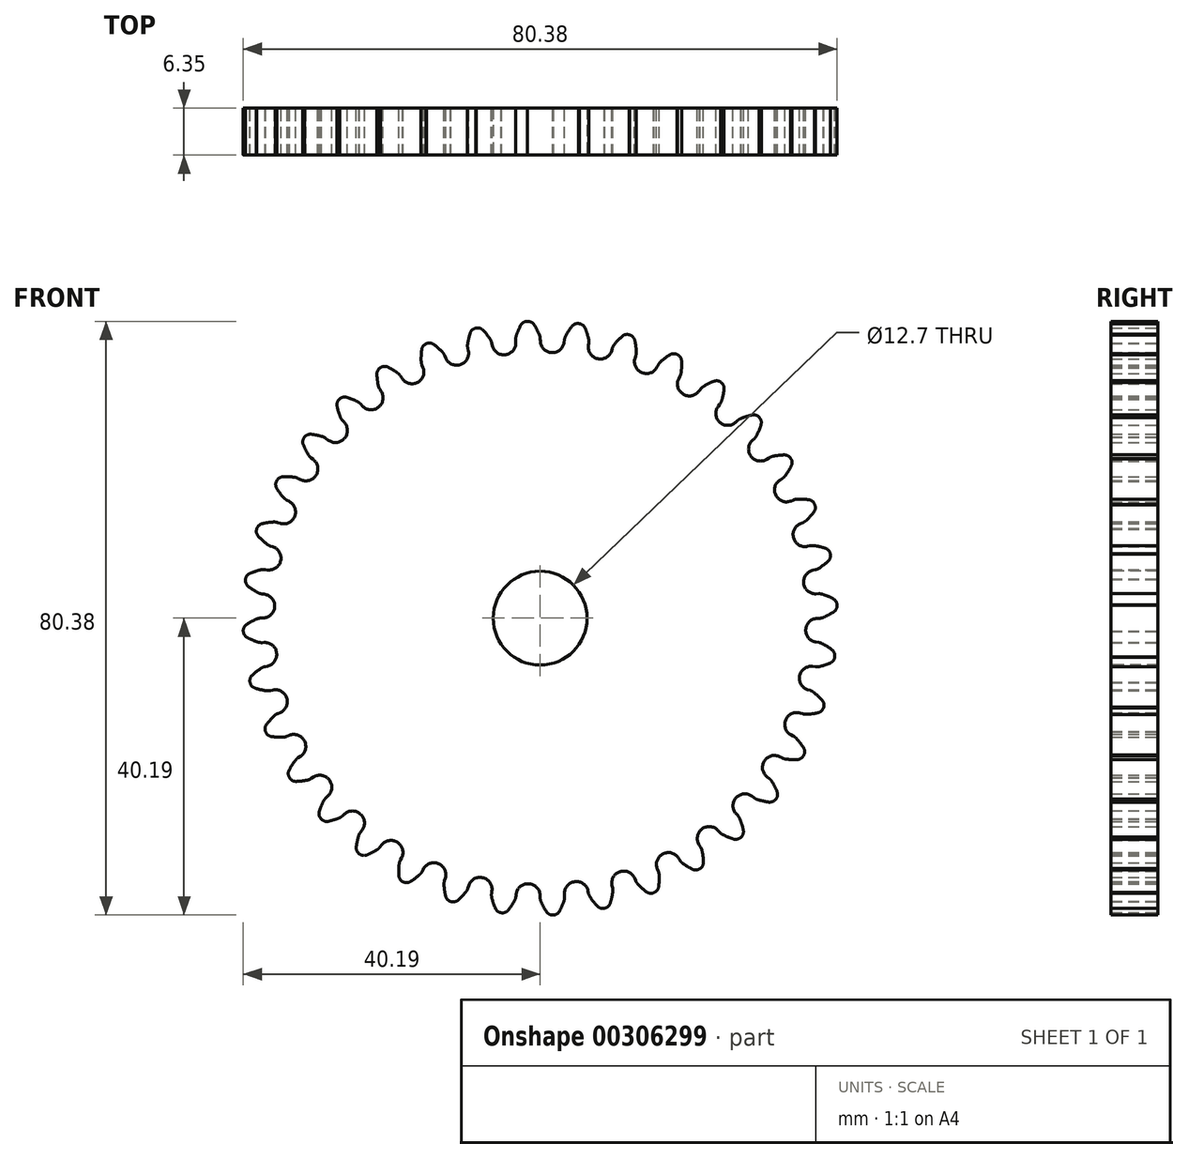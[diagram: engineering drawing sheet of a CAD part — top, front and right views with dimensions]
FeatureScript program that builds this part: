
annotation { "Feature Type Name" : "Feature", "Feature Type Description" : "" }
export const myFeature = defineFeature(function(context is Context, id is Id, definition is map)
    precondition{}
    {
        {
            var Q0;
            Q0=qCreatedBy(makeId("Front.planeOp"),FACE);
            var sketch = newSketch(context, id + "F0", { "sketchPlane" : qUnion([Q0])});
            skArc(sketch, "E0", {"start": v(-4.68, 35.67) * mm, "mid": v(-4.7, 35.67) * mm, "end": v(-4.7, 35.67) * mm});
            skArc(sketch, "E1.trimOffspring", {"start": v(-0.12, 38.39) * mm, "mid": v(-0.45, 39.07) * mm, "end": v(-0.83, 39.72) * mm});
            skLineSegment(sketch, "E2", {"start": v(-1.72, 40.19) * mm, "end": v(-1.75, 40.19) * mm});
            skLineSegment(sketch, "E3", {"start": v(0.01, 37.82) * mm, "end": v(0.03, 37.47) * mm});
            skLineSegment(sketch, "E4.MirrorCS", {"start": v(-1.8, 40.18) * mm, "end": v(-1.75, 40.19) * mm});
            skArc(sketch, "E5.MirrorCS", {"start": v(-3.23, 38.25) * mm, "mid": v(-2.96, 38.96) * mm, "end": v(-2.63, 39.64) * mm});
            skLineSegment(sketch, "E6.MirrorCS", {"start": v(-3.3, 37.67) * mm, "end": v(-3.3, 37.33) * mm});
            skPoint(sketch, "E7.visualSharp", {"position": v(-3.23, 35.83) * mm});
            skArc(sketch, "E7.filletArc", {"start": v(-4.68, 35.67) * mm, "mid": v(-3.67, 36.23) * mm, "end": v(-3.3, 37.33) * mm});
            skPoint(sketch, "E8.visualSharp", {"position": v(0.1, 35.98) * mm});
            skArc(sketch, "E8.filletArc", {"start": v(0.03, 37.47) * mm, "mid": v(0.5, 36.41) * mm, "end": v(1.56, 35.95) * mm});
            skPoint(sketch, "E9.visualSharp", {"position": v(-2.35, 40.15) * mm});
            skArc(sketch, "E9.filletArc", {"start": v(-1.8, 40.18) * mm, "mid": v(-2.28, 40.02) * mm, "end": v(-2.63, 39.64) * mm});
            skPoint(sketch, "E10.visualSharp", {"position": v(-1.16, 40.2) * mm});
            skArc(sketch, "E10.filletArc", {"start": v(-0.83, 39.72) * mm, "mid": v(-1.21, 40.07) * mm, "end": v(-1.72, 40.19) * mm});
            skPoint(sketch, "E11.visualSharp", {"position": v(0, 38.1) * mm});
            skArc(sketch, "E11.filletArc", {"start": v(0.01, 37.82) * mm, "mid": v(-0.03, 38.1) * mm, "end": v(-0.12, 38.39) * mm});
            skPoint(sketch, "E12.visualSharp", {"position": v(-3.32, 37.96) * mm});
            skArc(sketch, "E12.filletArc", {"start": v(-3.23, 38.25) * mm, "mid": v(-3.3, 37.97) * mm, "end": v(-3.3, 37.67) * mm});
            skArc(sketch, "E13.1.0", {"start": v(-6.78, 37.78) * mm, "mid": v(-7.23, 38.4) * mm, "end": v(-7.72, 38.97) * mm});
            skArc(sketch, "E13.1.1", {"start": v(-7.72, 38.97) * mm, "mid": v(-8.15, 39.25) * mm, "end": v(-8.67, 39.28) * mm});
            skArc(sketch, "E13.1.2", {"start": v(-8.74, 39.26) * mm, "mid": v(-9.2, 39.02) * mm, "end": v(-9.48, 38.58) * mm});
            skArc(sketch, "E13.1.3", {"start": v(-9.82, 37.1) * mm, "mid": v(-9.68, 37.85) * mm, "end": v(-9.48, 38.58) * mm});
            skArc(sketch, "E13.1.4", {"start": v(-10.8, 34.32) * mm, "mid": v(-9.9, 35.04) * mm, "end": v(-9.73, 36.2) * mm});
            skArc(sketch, "E13.1.5", {"start": v(-6.48, 36.9) * mm, "mid": v(-5.84, 35.95) * mm, "end": v(-4.7, 35.67) * mm});
            skArc(sketch, "E13.1.6", {"start": v(-9.82, 37.1) * mm, "mid": v(-9.84, 36.82) * mm, "end": v(-9.8, 36.53) * mm});
            skLineSegment(sketch, "E13.1.7", {"start": v(-9.8, 36.53) * mm, "end": v(-9.73, 36.2) * mm});
            skArc(sketch, "E13.1.8", {"start": v(-6.55, 37.24) * mm, "mid": v(-6.64, 37.52) * mm, "end": v(-6.78, 37.78) * mm});
            skLineSegment(sketch, "E13.1.9", {"start": v(-6.55, 37.24) * mm, "end": v(-6.48, 36.9) * mm});
            skArc(sketch, "E13.2.0", {"start": v(-13.24, 36.03) * mm, "mid": v(-13.78, 36.56) * mm, "end": v(-14.37, 37.04) * mm});
            skArc(sketch, "E13.2.1", {"start": v(-14.37, 37.04) * mm, "mid": v(-14.84, 37.24) * mm, "end": v(-15.36, 37.18) * mm});
            skArc(sketch, "E13.2.2", {"start": v(-15.43, 37.15) * mm, "mid": v(-15.84, 36.83) * mm, "end": v(-16.03, 36.35) * mm});
            skArc(sketch, "E13.2.3", {"start": v(-16.11, 34.84) * mm, "mid": v(-16.1, 35.6) * mm, "end": v(-16.03, 36.35) * mm});
            skArc(sketch, "E13.2.4", {"start": v(-16.6, 31.92) * mm, "mid": v(-15.84, 32.8) * mm, "end": v(-15.86, 33.95) * mm});
            skArc(sketch, "E13.2.5", {"start": v(-12.8, 35.22) * mm, "mid": v(-11.99, 34.39) * mm, "end": v(-10.83, 34.31) * mm});
            skArc(sketch, "E13.2.6", {"start": v(-16.11, 34.84) * mm, "mid": v(-16.08, 34.55) * mm, "end": v(-16, 34.27) * mm});
            skLineSegment(sketch, "E13.2.7", {"start": v(-16, 34.27) * mm, "end": v(-15.86, 33.95) * mm});
            skArc(sketch, "E13.2.8", {"start": v(-12.92, 35.54) * mm, "mid": v(-13.06, 35.8) * mm, "end": v(-13.24, 36.03) * mm});
            skLineSegment(sketch, "E13.2.9", {"start": v(-12.92, 35.54) * mm, "end": v(-12.8, 35.22) * mm});
            skArc(sketch, "E13.3.0", {"start": v(-19.3, 33.18) * mm, "mid": v(-19.92, 33.6) * mm, "end": v(-20.58, 33.98) * mm});
            skArc(sketch, "E13.3.1", {"start": v(-20.58, 33.98) * mm, "mid": v(-21.09, 34.1) * mm, "end": v(-21.58, 33.95) * mm});
            skArc(sketch, "E13.3.2", {"start": v(-21.64, 33.9) * mm, "mid": v(-22, 33.52) * mm, "end": v(-22.1, 33.01) * mm});
            skArc(sketch, "E13.3.3", {"start": v(-21.92, 31.51) * mm, "mid": v(-22.04, 32.26) * mm, "end": v(-22.1, 33.01) * mm});
            skArc(sketch, "E13.3.4", {"start": v(-21.9, 28.55) * mm, "mid": v(-21.3, 29.54) * mm, "end": v(-21.52, 30.68) * mm});
            skArc(sketch, "E13.3.5", {"start": v(-18.71, 32.47) * mm, "mid": v(-17.78, 31.78) * mm, "end": v(-16.62, 31.9) * mm});
            skArc(sketch, "E13.3.6", {"start": v(-21.92, 31.51) * mm, "mid": v(-21.84, 31.23) * mm, "end": v(-21.7, 30.97) * mm});
            skLineSegment(sketch, "E13.3.7", {"start": v(-21.7, 30.97) * mm, "end": v(-21.52, 30.68) * mm});
            skArc(sketch, "E13.3.8", {"start": v(-18.9, 32.76) * mm, "mid": v(-19.08, 32.99) * mm, "end": v(-19.3, 33.18) * mm});
            skLineSegment(sketch, "E13.3.9", {"start": v(-18.9, 32.76) * mm, "end": v(-18.71, 32.47) * mm});
            skArc(sketch, "E13.4.0", {"start": v(-24.77, 29.33) * mm, "mid": v(-25.46, 29.64) * mm, "end": v(-26.17, 29.9) * mm});
            skArc(sketch, "E13.4.1", {"start": v(-26.17, 29.9) * mm, "mid": v(-26.69, 29.92) * mm, "end": v(-27.15, 29.68) * mm});
            skArc(sketch, "E13.4.2", {"start": v(-27.2, 29.63) * mm, "mid": v(-27.48, 29.2) * mm, "end": v(-27.5, 28.68) * mm});
            skArc(sketch, "E13.4.3", {"start": v(-27.06, 27.23) * mm, "mid": v(-27.3, 27.94) * mm, "end": v(-27.5, 28.68) * mm});
            skArc(sketch, "E13.4.4", {"start": v(-26.52, 24.32) * mm, "mid": v(-26.1, 25.4) * mm, "end": v(-26.52, 26.48) * mm});
            skArc(sketch, "E13.4.5", {"start": v(-24.07, 28.72) * mm, "mid": v(-23.03, 28.21) * mm, "end": v(-21.91, 28.54) * mm});
            skArc(sketch, "E13.4.6", {"start": v(-27.06, 27.23) * mm, "mid": v(-26.93, 26.97) * mm, "end": v(-26.75, 26.73) * mm});
            skLineSegment(sketch, "E13.4.7", {"start": v(-26.75, 26.73) * mm, "end": v(-26.52, 26.48) * mm});
            skArc(sketch, "E13.4.8", {"start": v(-24.3, 28.98) * mm, "mid": v(-24.52, 29.17) * mm, "end": v(-24.77, 29.33) * mm});
            skLineSegment(sketch, "E13.4.9", {"start": v(-24.3, 28.98) * mm, "end": v(-24.07, 28.72) * mm});
            skArc(sketch, "E13.5.0", {"start": v(-29.48, 24.58) * mm, "mid": v(-30.22, 24.77) * mm, "end": v(-30.96, 24.9) * mm});
            skArc(sketch, "E13.5.1", {"start": v(-30.96, 24.9) * mm, "mid": v(-31.48, 24.83) * mm, "end": v(-31.89, 24.52) * mm});
            skArc(sketch, "E13.5.2", {"start": v(-31.94, 24.46) * mm, "mid": v(-32.13, 23.98) * mm, "end": v(-32.06, 23.46) * mm});
            skArc(sketch, "E13.5.3", {"start": v(-31.38, 22.12) * mm, "mid": v(-31.74, 22.78) * mm, "end": v(-32.06, 23.46) * mm});
            skArc(sketch, "E13.5.4", {"start": v(-30.34, 19.34) * mm, "mid": v(-30.11, 20.48) * mm, "end": v(-30.71, 21.47) * mm});
            skArc(sketch, "E13.5.5", {"start": v(-28.69, 24.1) * mm, "mid": v(-27.58, 23.78) * mm, "end": v(-26.54, 24.3) * mm});
            skArc(sketch, "E13.5.6", {"start": v(-31.38, 22.12) * mm, "mid": v(-31.2, 21.88) * mm, "end": v(-30.98, 21.68) * mm});
            skLineSegment(sketch, "E13.5.7", {"start": v(-30.98, 21.68) * mm, "end": v(-30.71, 21.47) * mm});
            skArc(sketch, "E13.5.8", {"start": v(-28.96, 24.32) * mm, "mid": v(-29.2, 24.47) * mm, "end": v(-29.48, 24.58) * mm});
            skLineSegment(sketch, "E13.5.9", {"start": v(-28.96, 24.32) * mm, "end": v(-28.69, 24.1) * mm});
            skArc(sketch, "E13.6.0", {"start": v(-33.3, 19.09) * mm, "mid": v(-34.06, 19.14) * mm, "end": v(-34.82, 19.14) * mm});
            skArc(sketch, "E13.6.1", {"start": v(-34.82, 19.14) * mm, "mid": v(-35.3, 18.99) * mm, "end": v(-35.66, 18.6) * mm});
            skArc(sketch, "E13.6.2", {"start": v(-35.7, 18.54) * mm, "mid": v(-35.8, 18.03) * mm, "end": v(-35.65, 17.54) * mm});
            skArc(sketch, "E13.6.3", {"start": v(-34.74, 16.33) * mm, "mid": v(-35.22, 16.92) * mm, "end": v(-35.65, 17.54) * mm});
            skArc(sketch, "E13.6.4", {"start": v(-33.24, 13.78) * mm, "mid": v(-33.2, 14.94) * mm, "end": v(-33.97, 15.81) * mm});
            skArc(sketch, "E13.6.5", {"start": v(-32.44, 18.76) * mm, "mid": v(-31.29, 18.63) * mm, "end": v(-30.35, 19.32) * mm});
            skArc(sketch, "E13.6.6", {"start": v(-34.74, 16.33) * mm, "mid": v(-34.53, 16.13) * mm, "end": v(-34.28, 15.97) * mm});
            skLineSegment(sketch, "E13.6.7", {"start": v(-34.28, 15.97) * mm, "end": v(-33.97, 15.81) * mm});
            skArc(sketch, "E13.6.8", {"start": v(-32.74, 18.92) * mm, "mid": v(-33.02, 19.03) * mm, "end": v(-33.3, 19.09) * mm});
            skLineSegment(sketch, "E13.6.9", {"start": v(-32.74, 18.92) * mm, "end": v(-32.44, 18.76) * mm});
            skArc(sketch, "E13.7.0", {"start": v(-36.11, 13.02) * mm, "mid": v(-36.87, 12.94) * mm, "end": v(-37.6, 12.8) * mm});
            skArc(sketch, "E13.7.1", {"start": v(-37.6, 12.8) * mm, "mid": v(-38.07, 12.57) * mm, "end": v(-38.35, 12.13) * mm});
            skArc(sketch, "E13.7.2", {"start": v(-38.37, 12.06) * mm, "mid": v(-38.4, 11.54) * mm, "end": v(-38.15, 11.08) * mm});
            skArc(sketch, "E13.7.3", {"start": v(-37.05, 10.05) * mm, "mid": v(-37.62, 10.55) * mm, "end": v(-38.15, 11.08) * mm});
            skArc(sketch, "E13.7.4", {"start": v(-35.12, 7.8) * mm, "mid": v(-35.3, 8.95) * mm, "end": v(-36.2, 9.67) * mm});
            skArc(sketch, "E13.7.5", {"start": v(-35.2, 12.84) * mm, "mid": v(-34.05, 12.92) * mm, "end": v(-33.25, 13.76) * mm});
            skArc(sketch, "E13.7.6", {"start": v(-37.05, 10.05) * mm, "mid": v(-36.8, 9.89) * mm, "end": v(-36.53, 9.78) * mm});
            skLineSegment(sketch, "E13.7.7", {"start": v(-36.53, 9.78) * mm, "end": v(-36.2, 9.67) * mm});
            skArc(sketch, "E13.7.8", {"start": v(-35.53, 12.95) * mm, "mid": v(-35.82, 13) * mm, "end": v(-36.11, 13.02) * mm});
            skLineSegment(sketch, "E13.7.9", {"start": v(-35.53, 12.95) * mm, "end": v(-35.2, 12.84) * mm});
            skArc(sketch, "E13.8.0", {"start": v(-37.82, 6.55) * mm, "mid": v(-38.55, 6.34) * mm, "end": v(-39.26, 6.08) * mm});
            skArc(sketch, "E13.8.1", {"start": v(-39.26, 6.08) * mm, "mid": v(-39.67, 5.76) * mm, "end": v(-39.88, 5.29) * mm});
            skArc(sketch, "E13.8.2", {"start": v(-39.89, 5.21) * mm, "mid": v(-39.81, 4.7) * mm, "end": v(-39.5, 4.3) * mm});
            skArc(sketch, "E13.8.3", {"start": v(-38.23, 3.46) * mm, "mid": v(-38.88, 3.85) * mm, "end": v(-39.5, 4.3) * mm});
            skArc(sketch, "E13.8.4", {"start": v(-35.94, 1.58) * mm, "mid": v(-36.32, 2.68) * mm, "end": v(-37.33, 3.24) * mm});
            skArc(sketch, "E13.8.5", {"start": v(-36.9, 6.53) * mm, "mid": v(-35.77, 6.81) * mm, "end": v(-35.13, 7.77) * mm});
            skArc(sketch, "E13.8.6", {"start": v(-38.23, 3.46) * mm, "mid": v(-37.96, 3.35) * mm, "end": v(-37.67, 3.28) * mm});
            skLineSegment(sketch, "E13.8.7", {"start": v(-37.67, 3.28) * mm, "end": v(-37.33, 3.24) * mm});
            skArc(sketch, "E13.8.8", {"start": v(-37.24, 6.58) * mm, "mid": v(-37.53, 6.6) * mm, "end": v(-37.82, 6.55) * mm});
            skLineSegment(sketch, "E13.8.9", {"start": v(-37.24, 6.58) * mm, "end": v(-36.9, 6.53) * mm});
            skArc(sketch, "E13.9.0", {"start": v(-38.39, -0.12) * mm, "mid": v(-39.07, -0.45) * mm, "end": v(-39.72, -0.83) * mm});
            skArc(sketch, "E13.9.1", {"start": v(-39.72, -0.83) * mm, "mid": v(-40.07, -1.21) * mm, "end": v(-40.19, -1.72) * mm});
            skArc(sketch, "E13.9.2", {"start": v(-40.18, -1.8) * mm, "mid": v(-40.02, -2.28) * mm, "end": v(-39.64, -2.63) * mm});
            skArc(sketch, "E13.9.3", {"start": v(-38.25, -3.23) * mm, "mid": v(-38.96, -2.96) * mm, "end": v(-39.64, -2.63) * mm});
            skArc(sketch, "E13.9.4", {"start": v(-35.67, -4.68) * mm, "mid": v(-36.23, -3.67) * mm, "end": v(-37.33, -3.3) * mm});
            skArc(sketch, "E13.9.5", {"start": v(-37.47, 0.03) * mm, "mid": v(-36.41, 0.5) * mm, "end": v(-35.95, 1.56) * mm});
            skArc(sketch, "E13.9.6", {"start": v(-38.25, -3.23) * mm, "mid": v(-37.97, -3.3) * mm, "end": v(-37.67, -3.3) * mm});
            skLineSegment(sketch, "E13.9.7", {"start": v(-37.67, -3.3) * mm, "end": v(-37.33, -3.3) * mm});
            skArc(sketch, "E13.9.8", {"start": v(-37.82, 0.01) * mm, "mid": v(-38.1, -0.03) * mm, "end": v(-38.39, -0.12) * mm});
            skLineSegment(sketch, "E13.9.9", {"start": v(-37.82, 0.01) * mm, "end": v(-37.47, 0.03) * mm});
            skArc(sketch, "E13.10.0", {"start": v(-37.78, -6.78) * mm, "mid": v(-38.4, -7.23) * mm, "end": v(-38.97, -7.72) * mm});
            skArc(sketch, "E13.10.1", {"start": v(-38.97, -7.72) * mm, "mid": v(-39.25, -8.15) * mm, "end": v(-39.28, -8.67) * mm});
            skArc(sketch, "E13.10.2", {"start": v(-39.26, -8.74) * mm, "mid": v(-39.02, -9.2) * mm, "end": v(-38.58, -9.48) * mm});
            skArc(sketch, "E13.10.3", {"start": v(-37.1, -9.82) * mm, "mid": v(-37.85, -9.68) * mm, "end": v(-38.58, -9.48) * mm});
            skArc(sketch, "E13.10.4", {"start": v(-34.32, -10.8) * mm, "mid": v(-35.04, -9.9) * mm, "end": v(-36.2, -9.73) * mm});
            skArc(sketch, "E13.10.5", {"start": v(-36.9, -6.48) * mm, "mid": v(-35.95, -5.84) * mm, "end": v(-35.67, -4.7) * mm});
            skArc(sketch, "E13.10.6", {"start": v(-37.1, -9.82) * mm, "mid": v(-36.82, -9.84) * mm, "end": v(-36.53, -9.8) * mm});
            skLineSegment(sketch, "E13.10.7", {"start": v(-36.53, -9.8) * mm, "end": v(-36.2, -9.73) * mm});
            skArc(sketch, "E13.10.8", {"start": v(-37.24, -6.55) * mm, "mid": v(-37.52, -6.64) * mm, "end": v(-37.78, -6.78) * mm});
            skLineSegment(sketch, "E13.10.9", {"start": v(-37.24, -6.55) * mm, "end": v(-36.9, -6.48) * mm});
            skArc(sketch, "E13.11.0", {"start": v(-36.03, -13.24) * mm, "mid": v(-36.56, -13.78) * mm, "end": v(-37.04, -14.37) * mm});
            skArc(sketch, "E13.11.1", {"start": v(-37.04, -14.37) * mm, "mid": v(-37.24, -14.84) * mm, "end": v(-37.18, -15.36) * mm});
            skArc(sketch, "E13.11.2", {"start": v(-37.15, -15.43) * mm, "mid": v(-36.83, -15.84) * mm, "end": v(-36.35, -16.03) * mm});
            skArc(sketch, "E13.11.3", {"start": v(-34.84, -16.11) * mm, "mid": v(-35.6, -16.1) * mm, "end": v(-36.35, -16.03) * mm});
            skArc(sketch, "E13.11.4", {"start": v(-31.92, -16.6) * mm, "mid": v(-32.8, -15.84) * mm, "end": v(-33.95, -15.86) * mm});
            skArc(sketch, "E13.11.5", {"start": v(-35.22, -12.8) * mm, "mid": v(-34.39, -11.99) * mm, "end": v(-34.31, -10.83) * mm});
            skArc(sketch, "E13.11.6", {"start": v(-34.84, -16.11) * mm, "mid": v(-34.55, -16.08) * mm, "end": v(-34.27, -16) * mm});
            skLineSegment(sketch, "E13.11.7", {"start": v(-34.27, -16) * mm, "end": v(-33.95, -15.86) * mm});
            skArc(sketch, "E13.11.8", {"start": v(-35.54, -12.92) * mm, "mid": v(-35.8, -13.06) * mm, "end": v(-36.03, -13.24) * mm});
            skLineSegment(sketch, "E13.11.9", {"start": v(-35.54, -12.92) * mm, "end": v(-35.22, -12.8) * mm});
            skArc(sketch, "E13.12.0", {"start": v(-33.18, -19.3) * mm, "mid": v(-33.6, -19.92) * mm, "end": v(-33.98, -20.58) * mm});
            skArc(sketch, "E13.12.1", {"start": v(-33.98, -20.58) * mm, "mid": v(-34.1, -21.09) * mm, "end": v(-33.95, -21.58) * mm});
            skArc(sketch, "E13.12.2", {"start": v(-33.9, -21.64) * mm, "mid": v(-33.52, -22) * mm, "end": v(-33.01, -22.1) * mm});
            skArc(sketch, "E13.12.3", {"start": v(-31.51, -21.92) * mm, "mid": v(-32.26, -22.04) * mm, "end": v(-33.01, -22.1) * mm});
            skArc(sketch, "E13.12.4", {"start": v(-28.55, -21.9) * mm, "mid": v(-29.54, -21.3) * mm, "end": v(-30.68, -21.52) * mm});
            skArc(sketch, "E13.12.5", {"start": v(-32.47, -18.71) * mm, "mid": v(-31.78, -17.78) * mm, "end": v(-31.9, -16.62) * mm});
            skArc(sketch, "E13.12.6", {"start": v(-31.51, -21.92) * mm, "mid": v(-31.23, -21.84) * mm, "end": v(-30.97, -21.7) * mm});
            skLineSegment(sketch, "E13.12.7", {"start": v(-30.97, -21.7) * mm, "end": v(-30.68, -21.52) * mm});
            skArc(sketch, "E13.12.8", {"start": v(-32.76, -18.9) * mm, "mid": v(-32.99, -19.08) * mm, "end": v(-33.18, -19.3) * mm});
            skLineSegment(sketch, "E13.12.9", {"start": v(-32.76, -18.9) * mm, "end": v(-32.47, -18.71) * mm});
            skArc(sketch, "E13.13.0", {"start": v(-29.33, -24.77) * mm, "mid": v(-29.64, -25.46) * mm, "end": v(-29.9, -26.17) * mm});
            skArc(sketch, "E13.13.1", {"start": v(-29.9, -26.17) * mm, "mid": v(-29.92, -26.69) * mm, "end": v(-29.68, -27.15) * mm});
            skArc(sketch, "E13.13.2", {"start": v(-29.63, -27.2) * mm, "mid": v(-29.2, -27.48) * mm, "end": v(-28.68, -27.5) * mm});
            skArc(sketch, "E13.13.3", {"start": v(-27.23, -27.06) * mm, "mid": v(-27.94, -27.3) * mm, "end": v(-28.68, -27.5) * mm});
            skArc(sketch, "E13.13.4", {"start": v(-24.32, -26.52) * mm, "mid": v(-25.4, -26.1) * mm, "end": v(-26.48, -26.52) * mm});
            skArc(sketch, "E13.13.5", {"start": v(-28.72, -24.07) * mm, "mid": v(-28.21, -23.03) * mm, "end": v(-28.54, -21.91) * mm});
            skArc(sketch, "E13.13.6", {"start": v(-27.23, -27.06) * mm, "mid": v(-26.97, -26.93) * mm, "end": v(-26.73, -26.75) * mm});
            skLineSegment(sketch, "E13.13.7", {"start": v(-26.73, -26.75) * mm, "end": v(-26.48, -26.52) * mm});
            skArc(sketch, "E13.13.8", {"start": v(-28.98, -24.3) * mm, "mid": v(-29.17, -24.52) * mm, "end": v(-29.33, -24.77) * mm});
            skLineSegment(sketch, "E13.13.9", {"start": v(-28.98, -24.3) * mm, "end": v(-28.72, -24.07) * mm});
            skArc(sketch, "E13.14.0", {"start": v(-24.58, -29.48) * mm, "mid": v(-24.77, -30.22) * mm, "end": v(-24.9, -30.96) * mm});
            skArc(sketch, "E13.14.1", {"start": v(-24.9, -30.96) * mm, "mid": v(-24.83, -31.48) * mm, "end": v(-24.52, -31.89) * mm});
            skArc(sketch, "E13.14.2", {"start": v(-24.46, -31.94) * mm, "mid": v(-23.98, -32.13) * mm, "end": v(-23.46, -32.06) * mm});
            skArc(sketch, "E13.14.3", {"start": v(-22.12, -31.38) * mm, "mid": v(-22.78, -31.74) * mm, "end": v(-23.46, -32.06) * mm});
            skArc(sketch, "E13.14.4", {"start": v(-19.34, -30.34) * mm, "mid": v(-20.48, -30.11) * mm, "end": v(-21.47, -30.71) * mm});
            skArc(sketch, "E13.14.5", {"start": v(-24.1, -28.69) * mm, "mid": v(-23.78, -27.58) * mm, "end": v(-24.3, -26.54) * mm});
            skArc(sketch, "E13.14.6", {"start": v(-22.12, -31.38) * mm, "mid": v(-21.88, -31.2) * mm, "end": v(-21.68, -30.98) * mm});
            skLineSegment(sketch, "E13.14.7", {"start": v(-21.68, -30.98) * mm, "end": v(-21.47, -30.71) * mm});
            skArc(sketch, "E13.14.8", {"start": v(-24.32, -28.96) * mm, "mid": v(-24.47, -29.2) * mm, "end": v(-24.58, -29.48) * mm});
            skLineSegment(sketch, "E13.14.9", {"start": v(-24.32, -28.96) * mm, "end": v(-24.1, -28.69) * mm});
            skArc(sketch, "E13.15.0", {"start": v(-19.09, -33.3) * mm, "mid": v(-19.14, -34.06) * mm, "end": v(-19.14, -34.82) * mm});
            skArc(sketch, "E13.15.1", {"start": v(-19.14, -34.82) * mm, "mid": v(-18.99, -35.3) * mm, "end": v(-18.6, -35.66) * mm});
            skArc(sketch, "E13.15.2", {"start": v(-18.54, -35.7) * mm, "mid": v(-18.03, -35.8) * mm, "end": v(-17.54, -35.65) * mm});
            skArc(sketch, "E13.15.3", {"start": v(-16.33, -34.74) * mm, "mid": v(-16.92, -35.22) * mm, "end": v(-17.54, -35.65) * mm});
            skArc(sketch, "E13.15.4", {"start": v(-13.78, -33.24) * mm, "mid": v(-14.94, -33.2) * mm, "end": v(-15.81, -33.97) * mm});
            skArc(sketch, "E13.15.5", {"start": v(-18.76, -32.44) * mm, "mid": v(-18.63, -31.29) * mm, "end": v(-19.32, -30.35) * mm});
            skArc(sketch, "E13.15.6", {"start": v(-16.33, -34.74) * mm, "mid": v(-16.13, -34.53) * mm, "end": v(-15.97, -34.28) * mm});
            skLineSegment(sketch, "E13.15.7", {"start": v(-15.97, -34.28) * mm, "end": v(-15.81, -33.97) * mm});
            skArc(sketch, "E13.15.8", {"start": v(-18.92, -32.74) * mm, "mid": v(-19.03, -33.02) * mm, "end": v(-19.09, -33.3) * mm});
            skLineSegment(sketch, "E13.15.9", {"start": v(-18.92, -32.74) * mm, "end": v(-18.76, -32.44) * mm});
            skArc(sketch, "E13.16.0", {"start": v(-13.02, -36.11) * mm, "mid": v(-12.94, -36.87) * mm, "end": v(-12.8, -37.6) * mm});
            skArc(sketch, "E13.16.1", {"start": v(-12.8, -37.6) * mm, "mid": v(-12.57, -38.07) * mm, "end": v(-12.13, -38.35) * mm});
            skArc(sketch, "E13.16.2", {"start": v(-12.06, -38.37) * mm, "mid": v(-11.54, -38.4) * mm, "end": v(-11.08, -38.15) * mm});
            skArc(sketch, "E13.16.3", {"start": v(-10.05, -37.05) * mm, "mid": v(-10.55, -37.62) * mm, "end": v(-11.08, -38.15) * mm});
            skArc(sketch, "E13.16.4", {"start": v(-7.8, -35.12) * mm, "mid": v(-8.95, -35.3) * mm, "end": v(-9.67, -36.2) * mm});
            skArc(sketch, "E13.16.5", {"start": v(-12.84, -35.2) * mm, "mid": v(-12.92, -34.05) * mm, "end": v(-13.76, -33.25) * mm});
            skArc(sketch, "E13.16.6", {"start": v(-10.05, -37.05) * mm, "mid": v(-9.89, -36.8) * mm, "end": v(-9.78, -36.53) * mm});
            skLineSegment(sketch, "E13.16.7", {"start": v(-9.78, -36.53) * mm, "end": v(-9.67, -36.2) * mm});
            skArc(sketch, "E13.16.8", {"start": v(-12.95, -35.53) * mm, "mid": v(-13, -35.82) * mm, "end": v(-13.02, -36.11) * mm});
            skLineSegment(sketch, "E13.16.9", {"start": v(-12.95, -35.53) * mm, "end": v(-12.84, -35.2) * mm});
            skArc(sketch, "E13.17.0", {"start": v(-6.55, -37.82) * mm, "mid": v(-6.34, -38.55) * mm, "end": v(-6.08, -39.26) * mm});
            skArc(sketch, "E13.17.1", {"start": v(-6.08, -39.26) * mm, "mid": v(-5.76, -39.67) * mm, "end": v(-5.29, -39.88) * mm});
            skArc(sketch, "E13.17.2", {"start": v(-5.21, -39.89) * mm, "mid": v(-4.7, -39.81) * mm, "end": v(-4.3, -39.5) * mm});
            skArc(sketch, "E13.17.3", {"start": v(-3.46, -38.23) * mm, "mid": v(-3.85, -38.88) * mm, "end": v(-4.3, -39.5) * mm});
            skArc(sketch, "E13.17.4", {"start": v(-1.58, -35.94) * mm, "mid": v(-2.68, -36.32) * mm, "end": v(-3.24, -37.33) * mm});
            skArc(sketch, "E13.17.5", {"start": v(-6.53, -36.9) * mm, "mid": v(-6.81, -35.77) * mm, "end": v(-7.77, -35.13) * mm});
            skArc(sketch, "E13.17.6", {"start": v(-3.46, -38.23) * mm, "mid": v(-3.35, -37.96) * mm, "end": v(-3.28, -37.67) * mm});
            skLineSegment(sketch, "E13.17.7", {"start": v(-3.28, -37.67) * mm, "end": v(-3.24, -37.33) * mm});
            skArc(sketch, "E13.17.8", {"start": v(-6.58, -37.24) * mm, "mid": v(-6.6, -37.53) * mm, "end": v(-6.55, -37.82) * mm});
            skLineSegment(sketch, "E13.17.9", {"start": v(-6.58, -37.24) * mm, "end": v(-6.53, -36.9) * mm});
            skArc(sketch, "E13.18.0", {"start": v(0.12, -38.39) * mm, "mid": v(0.45, -39.07) * mm, "end": v(0.83, -39.72) * mm});
            skArc(sketch, "E13.18.1", {"start": v(0.83, -39.72) * mm, "mid": v(1.21, -40.07) * mm, "end": v(1.72, -40.19) * mm});
            skArc(sketch, "E13.18.2", {"start": v(1.8, -40.18) * mm, "mid": v(2.28, -40.02) * mm, "end": v(2.63, -39.64) * mm});
            skArc(sketch, "E13.18.3", {"start": v(3.23, -38.25) * mm, "mid": v(2.96, -38.96) * mm, "end": v(2.63, -39.64) * mm});
            skArc(sketch, "E13.18.4", {"start": v(4.68, -35.67) * mm, "mid": v(3.67, -36.23) * mm, "end": v(3.3, -37.33) * mm});
            skArc(sketch, "E13.18.5", {"start": v(-0.03, -37.47) * mm, "mid": v(-0.5, -36.41) * mm, "end": v(-1.56, -35.95) * mm});
            skArc(sketch, "E13.18.6", {"start": v(3.23, -38.25) * mm, "mid": v(3.3, -37.97) * mm, "end": v(3.3, -37.67) * mm});
            skLineSegment(sketch, "E13.18.7", {"start": v(3.3, -37.67) * mm, "end": v(3.3, -37.33) * mm});
            skArc(sketch, "E13.18.8", {"start": v(-0.01, -37.82) * mm, "mid": v(0.03, -38.1) * mm, "end": v(0.12, -38.39) * mm});
            skLineSegment(sketch, "E13.18.9", {"start": v(-0.01, -37.82) * mm, "end": v(-0.03, -37.47) * mm});
            skArc(sketch, "E13.19.0", {"start": v(6.78, -37.78) * mm, "mid": v(7.23, -38.4) * mm, "end": v(7.72, -38.97) * mm});
            skArc(sketch, "E13.19.1", {"start": v(7.72, -38.97) * mm, "mid": v(8.15, -39.25) * mm, "end": v(8.67, -39.28) * mm});
            skArc(sketch, "E13.19.2", {"start": v(8.74, -39.26) * mm, "mid": v(9.2, -39.02) * mm, "end": v(9.48, -38.58) * mm});
            skArc(sketch, "E13.19.3", {"start": v(9.82, -37.1) * mm, "mid": v(9.68, -37.85) * mm, "end": v(9.48, -38.58) * mm});
            skArc(sketch, "E13.19.4", {"start": v(10.8, -34.32) * mm, "mid": v(9.9, -35.04) * mm, "end": v(9.73, -36.2) * mm});
            skArc(sketch, "E13.19.5", {"start": v(6.48, -36.9) * mm, "mid": v(5.84, -35.95) * mm, "end": v(4.7, -35.67) * mm});
            skArc(sketch, "E13.19.6", {"start": v(9.82, -37.1) * mm, "mid": v(9.84, -36.82) * mm, "end": v(9.8, -36.53) * mm});
            skLineSegment(sketch, "E13.19.7", {"start": v(9.8, -36.53) * mm, "end": v(9.73, -36.2) * mm});
            skArc(sketch, "E13.19.8", {"start": v(6.55, -37.24) * mm, "mid": v(6.64, -37.52) * mm, "end": v(6.78, -37.78) * mm});
            skLineSegment(sketch, "E13.19.9", {"start": v(6.55, -37.24) * mm, "end": v(6.48, -36.9) * mm});
            skArc(sketch, "E13.20.0", {"start": v(13.24, -36.03) * mm, "mid": v(13.78, -36.56) * mm, "end": v(14.37, -37.04) * mm});
            skArc(sketch, "E13.20.1", {"start": v(14.37, -37.04) * mm, "mid": v(14.84, -37.24) * mm, "end": v(15.36, -37.18) * mm});
            skArc(sketch, "E13.20.2", {"start": v(15.43, -37.15) * mm, "mid": v(15.84, -36.83) * mm, "end": v(16.03, -36.35) * mm});
            skArc(sketch, "E13.20.3", {"start": v(16.11, -34.84) * mm, "mid": v(16.1, -35.6) * mm, "end": v(16.03, -36.35) * mm});
            skArc(sketch, "E13.20.4", {"start": v(16.6, -31.92) * mm, "mid": v(15.84, -32.8) * mm, "end": v(15.86, -33.95) * mm});
            skArc(sketch, "E13.20.5", {"start": v(12.8, -35.22) * mm, "mid": v(11.99, -34.39) * mm, "end": v(10.83, -34.31) * mm});
            skArc(sketch, "E13.20.6", {"start": v(16.11, -34.84) * mm, "mid": v(16.08, -34.55) * mm, "end": v(16, -34.27) * mm});
            skLineSegment(sketch, "E13.20.7", {"start": v(16, -34.27) * mm, "end": v(15.86, -33.95) * mm});
            skArc(sketch, "E13.20.8", {"start": v(12.92, -35.54) * mm, "mid": v(13.06, -35.8) * mm, "end": v(13.24, -36.03) * mm});
            skLineSegment(sketch, "E13.20.9", {"start": v(12.92, -35.54) * mm, "end": v(12.8, -35.22) * mm});
            skArc(sketch, "E13.21.0", {"start": v(19.3, -33.18) * mm, "mid": v(19.92, -33.6) * mm, "end": v(20.58, -33.98) * mm});
            skArc(sketch, "E13.21.1", {"start": v(20.58, -33.98) * mm, "mid": v(21.09, -34.1) * mm, "end": v(21.58, -33.95) * mm});
            skArc(sketch, "E13.21.2", {"start": v(21.64, -33.9) * mm, "mid": v(22, -33.52) * mm, "end": v(22.1, -33.01) * mm});
            skArc(sketch, "E13.21.3", {"start": v(21.92, -31.51) * mm, "mid": v(22.04, -32.26) * mm, "end": v(22.1, -33.01) * mm});
            skArc(sketch, "E13.21.4", {"start": v(21.9, -28.55) * mm, "mid": v(21.3, -29.54) * mm, "end": v(21.52, -30.68) * mm});
            skArc(sketch, "E13.21.5", {"start": v(18.71, -32.47) * mm, "mid": v(17.78, -31.78) * mm, "end": v(16.62, -31.9) * mm});
            skArc(sketch, "E13.21.6", {"start": v(21.92, -31.51) * mm, "mid": v(21.84, -31.23) * mm, "end": v(21.7, -30.97) * mm});
            skLineSegment(sketch, "E13.21.7", {"start": v(21.7, -30.97) * mm, "end": v(21.52, -30.68) * mm});
            skArc(sketch, "E13.21.8", {"start": v(18.9, -32.76) * mm, "mid": v(19.08, -32.99) * mm, "end": v(19.3, -33.18) * mm});
            skLineSegment(sketch, "E13.21.9", {"start": v(18.9, -32.76) * mm, "end": v(18.71, -32.47) * mm});
            skArc(sketch, "E13.22.0", {"start": v(24.77, -29.33) * mm, "mid": v(25.46, -29.64) * mm, "end": v(26.17, -29.9) * mm});
            skArc(sketch, "E13.22.1", {"start": v(26.17, -29.9) * mm, "mid": v(26.69, -29.92) * mm, "end": v(27.15, -29.68) * mm});
            skArc(sketch, "E13.22.2", {"start": v(27.2, -29.63) * mm, "mid": v(27.48, -29.2) * mm, "end": v(27.5, -28.68) * mm});
            skArc(sketch, "E13.22.3", {"start": v(27.06, -27.23) * mm, "mid": v(27.3, -27.94) * mm, "end": v(27.5, -28.68) * mm});
            skArc(sketch, "E13.22.4", {"start": v(26.52, -24.32) * mm, "mid": v(26.1, -25.4) * mm, "end": v(26.52, -26.48) * mm});
            skArc(sketch, "E13.22.5", {"start": v(24.07, -28.72) * mm, "mid": v(23.03, -28.21) * mm, "end": v(21.91, -28.54) * mm});
            skArc(sketch, "E13.22.6", {"start": v(27.06, -27.23) * mm, "mid": v(26.93, -26.97) * mm, "end": v(26.75, -26.73) * mm});
            skLineSegment(sketch, "E13.22.7", {"start": v(26.75, -26.73) * mm, "end": v(26.52, -26.48) * mm});
            skArc(sketch, "E13.22.8", {"start": v(24.3, -28.98) * mm, "mid": v(24.52, -29.17) * mm, "end": v(24.77, -29.33) * mm});
            skLineSegment(sketch, "E13.22.9", {"start": v(24.3, -28.98) * mm, "end": v(24.07, -28.72) * mm});
            skArc(sketch, "E13.23.0", {"start": v(29.48, -24.58) * mm, "mid": v(30.22, -24.77) * mm, "end": v(30.96, -24.9) * mm});
            skArc(sketch, "E13.23.1", {"start": v(30.96, -24.9) * mm, "mid": v(31.48, -24.83) * mm, "end": v(31.89, -24.52) * mm});
            skArc(sketch, "E13.23.2", {"start": v(31.94, -24.46) * mm, "mid": v(32.13, -23.98) * mm, "end": v(32.06, -23.46) * mm});
            skArc(sketch, "E13.23.3", {"start": v(31.38, -22.12) * mm, "mid": v(31.74, -22.78) * mm, "end": v(32.06, -23.46) * mm});
            skArc(sketch, "E13.23.4", {"start": v(30.34, -19.34) * mm, "mid": v(30.11, -20.48) * mm, "end": v(30.71, -21.47) * mm});
            skArc(sketch, "E13.23.5", {"start": v(28.69, -24.1) * mm, "mid": v(27.58, -23.78) * mm, "end": v(26.54, -24.3) * mm});
            skArc(sketch, "E13.23.6", {"start": v(31.38, -22.12) * mm, "mid": v(31.2, -21.88) * mm, "end": v(30.98, -21.68) * mm});
            skLineSegment(sketch, "E13.23.7", {"start": v(30.98, -21.68) * mm, "end": v(30.71, -21.47) * mm});
            skArc(sketch, "E13.23.8", {"start": v(28.96, -24.32) * mm, "mid": v(29.2, -24.47) * mm, "end": v(29.48, -24.58) * mm});
            skLineSegment(sketch, "E13.23.9", {"start": v(28.96, -24.32) * mm, "end": v(28.69, -24.1) * mm});
            skArc(sketch, "E13.24.0", {"start": v(33.3, -19.09) * mm, "mid": v(34.06, -19.14) * mm, "end": v(34.82, -19.14) * mm});
            skArc(sketch, "E13.24.1", {"start": v(34.82, -19.14) * mm, "mid": v(35.3, -18.99) * mm, "end": v(35.66, -18.6) * mm});
            skArc(sketch, "E13.24.2", {"start": v(35.7, -18.54) * mm, "mid": v(35.8, -18.03) * mm, "end": v(35.65, -17.54) * mm});
            skArc(sketch, "E13.24.3", {"start": v(34.74, -16.33) * mm, "mid": v(35.22, -16.92) * mm, "end": v(35.65, -17.54) * mm});
            skArc(sketch, "E13.24.4", {"start": v(33.24, -13.78) * mm, "mid": v(33.2, -14.94) * mm, "end": v(33.97, -15.81) * mm});
            skArc(sketch, "E13.24.5", {"start": v(32.44, -18.76) * mm, "mid": v(31.29, -18.63) * mm, "end": v(30.35, -19.32) * mm});
            skArc(sketch, "E13.24.6", {"start": v(34.74, -16.33) * mm, "mid": v(34.53, -16.13) * mm, "end": v(34.28, -15.97) * mm});
            skLineSegment(sketch, "E13.24.7", {"start": v(34.28, -15.97) * mm, "end": v(33.97, -15.81) * mm});
            skArc(sketch, "E13.24.8", {"start": v(32.74, -18.92) * mm, "mid": v(33.02, -19.03) * mm, "end": v(33.3, -19.09) * mm});
            skLineSegment(sketch, "E13.24.9", {"start": v(32.74, -18.92) * mm, "end": v(32.44, -18.76) * mm});
            skArc(sketch, "E13.25.0", {"start": v(36.11, -13.02) * mm, "mid": v(36.87, -12.94) * mm, "end": v(37.6, -12.8) * mm});
            skArc(sketch, "E13.25.1", {"start": v(37.6, -12.8) * mm, "mid": v(38.07, -12.57) * mm, "end": v(38.35, -12.13) * mm});
            skArc(sketch, "E13.25.2", {"start": v(38.37, -12.06) * mm, "mid": v(38.4, -11.54) * mm, "end": v(38.15, -11.08) * mm});
            skArc(sketch, "E13.25.3", {"start": v(37.05, -10.05) * mm, "mid": v(37.62, -10.55) * mm, "end": v(38.15, -11.08) * mm});
            skArc(sketch, "E13.25.4", {"start": v(35.12, -7.8) * mm, "mid": v(35.3, -8.95) * mm, "end": v(36.2, -9.67) * mm});
            skArc(sketch, "E13.25.5", {"start": v(35.2, -12.84) * mm, "mid": v(34.05, -12.92) * mm, "end": v(33.25, -13.76) * mm});
            skArc(sketch, "E13.25.6", {"start": v(37.05, -10.05) * mm, "mid": v(36.8, -9.89) * mm, "end": v(36.53, -9.78) * mm});
            skLineSegment(sketch, "E13.25.7", {"start": v(36.53, -9.78) * mm, "end": v(36.2, -9.67) * mm});
            skArc(sketch, "E13.25.8", {"start": v(35.53, -12.95) * mm, "mid": v(35.82, -13) * mm, "end": v(36.11, -13.02) * mm});
            skLineSegment(sketch, "E13.25.9", {"start": v(35.53, -12.95) * mm, "end": v(35.2, -12.84) * mm});
            skArc(sketch, "E13.26.0", {"start": v(37.82, -6.55) * mm, "mid": v(38.55, -6.34) * mm, "end": v(39.26, -6.08) * mm});
            skArc(sketch, "E13.26.1", {"start": v(39.26, -6.08) * mm, "mid": v(39.67, -5.76) * mm, "end": v(39.88, -5.29) * mm});
            skArc(sketch, "E13.26.2", {"start": v(39.89, -5.21) * mm, "mid": v(39.81, -4.7) * mm, "end": v(39.5, -4.3) * mm});
            skArc(sketch, "E13.26.3", {"start": v(38.23, -3.46) * mm, "mid": v(38.88, -3.85) * mm, "end": v(39.5, -4.3) * mm});
            skArc(sketch, "E13.26.4", {"start": v(35.94, -1.58) * mm, "mid": v(36.32, -2.68) * mm, "end": v(37.33, -3.24) * mm});
            skArc(sketch, "E13.26.5", {"start": v(36.9, -6.53) * mm, "mid": v(35.77, -6.81) * mm, "end": v(35.13, -7.77) * mm});
            skArc(sketch, "E13.26.6", {"start": v(38.23, -3.46) * mm, "mid": v(37.96, -3.35) * mm, "end": v(37.67, -3.28) * mm});
            skLineSegment(sketch, "E13.26.7", {"start": v(37.67, -3.28) * mm, "end": v(37.33, -3.24) * mm});
            skArc(sketch, "E13.26.8", {"start": v(37.24, -6.58) * mm, "mid": v(37.53, -6.6) * mm, "end": v(37.82, -6.55) * mm});
            skLineSegment(sketch, "E13.26.9", {"start": v(37.24, -6.58) * mm, "end": v(36.9, -6.53) * mm});
            skArc(sketch, "E13.27.0", {"start": v(38.39, 0.12) * mm, "mid": v(39.07, 0.45) * mm, "end": v(39.72, 0.83) * mm});
            skArc(sketch, "E13.27.1", {"start": v(39.72, 0.83) * mm, "mid": v(40.07, 1.21) * mm, "end": v(40.19, 1.72) * mm});
            skArc(sketch, "E13.27.2", {"start": v(40.18, 1.8) * mm, "mid": v(40.02, 2.28) * mm, "end": v(39.64, 2.63) * mm});
            skArc(sketch, "E13.27.3", {"start": v(38.25, 3.23) * mm, "mid": v(38.96, 2.96) * mm, "end": v(39.64, 2.63) * mm});
            skArc(sketch, "E13.27.4", {"start": v(35.67, 4.68) * mm, "mid": v(36.23, 3.67) * mm, "end": v(37.33, 3.3) * mm});
            skArc(sketch, "E13.27.5", {"start": v(37.47, -0.03) * mm, "mid": v(36.41, -0.5) * mm, "end": v(35.95, -1.56) * mm});
            skArc(sketch, "E13.27.6", {"start": v(38.25, 3.23) * mm, "mid": v(37.97, 3.3) * mm, "end": v(37.67, 3.3) * mm});
            skLineSegment(sketch, "E13.27.7", {"start": v(37.67, 3.3) * mm, "end": v(37.33, 3.3) * mm});
            skArc(sketch, "E13.27.8", {"start": v(37.82, -0.01) * mm, "mid": v(38.1, 0.03) * mm, "end": v(38.39, 0.12) * mm});
            skLineSegment(sketch, "E13.27.9", {"start": v(37.82, -0.01) * mm, "end": v(37.47, -0.03) * mm});
            skArc(sketch, "E13.28.0", {"start": v(37.78, 6.78) * mm, "mid": v(38.4, 7.23) * mm, "end": v(38.97, 7.72) * mm});
            skArc(sketch, "E13.28.1", {"start": v(38.97, 7.72) * mm, "mid": v(39.25, 8.15) * mm, "end": v(39.28, 8.67) * mm});
            skArc(sketch, "E13.28.2", {"start": v(39.26, 8.74) * mm, "mid": v(39.02, 9.2) * mm, "end": v(38.58, 9.48) * mm});
            skArc(sketch, "E13.28.3", {"start": v(37.1, 9.82) * mm, "mid": v(37.85, 9.68) * mm, "end": v(38.58, 9.48) * mm});
            skArc(sketch, "E13.28.4", {"start": v(34.32, 10.8) * mm, "mid": v(35.04, 9.9) * mm, "end": v(36.2, 9.73) * mm});
            skArc(sketch, "E13.28.5", {"start": v(36.9, 6.48) * mm, "mid": v(35.95, 5.84) * mm, "end": v(35.67, 4.7) * mm});
            skArc(sketch, "E13.28.6", {"start": v(37.1, 9.82) * mm, "mid": v(36.82, 9.84) * mm, "end": v(36.53, 9.8) * mm});
            skLineSegment(sketch, "E13.28.7", {"start": v(36.53, 9.8) * mm, "end": v(36.2, 9.73) * mm});
            skArc(sketch, "E13.28.8", {"start": v(37.24, 6.55) * mm, "mid": v(37.52, 6.64) * mm, "end": v(37.78, 6.78) * mm});
            skLineSegment(sketch, "E13.28.9", {"start": v(37.24, 6.55) * mm, "end": v(36.9, 6.48) * mm});
            skArc(sketch, "E13.29.0", {"start": v(36.03, 13.24) * mm, "mid": v(36.56, 13.78) * mm, "end": v(37.04, 14.37) * mm});
            skArc(sketch, "E13.29.1", {"start": v(37.04, 14.37) * mm, "mid": v(37.24, 14.84) * mm, "end": v(37.18, 15.36) * mm});
            skArc(sketch, "E13.29.2", {"start": v(37.15, 15.43) * mm, "mid": v(36.83, 15.84) * mm, "end": v(36.35, 16.03) * mm});
            skArc(sketch, "E13.29.3", {"start": v(34.84, 16.11) * mm, "mid": v(35.6, 16.1) * mm, "end": v(36.35, 16.03) * mm});
            skArc(sketch, "E13.29.4", {"start": v(31.92, 16.6) * mm, "mid": v(32.8, 15.84) * mm, "end": v(33.95, 15.86) * mm});
            skArc(sketch, "E13.29.5", {"start": v(35.22, 12.8) * mm, "mid": v(34.39, 11.99) * mm, "end": v(34.31, 10.83) * mm});
            skArc(sketch, "E13.29.6", {"start": v(34.84, 16.11) * mm, "mid": v(34.55, 16.08) * mm, "end": v(34.27, 16) * mm});
            skLineSegment(sketch, "E13.29.7", {"start": v(34.27, 16) * mm, "end": v(33.95, 15.86) * mm});
            skArc(sketch, "E13.29.8", {"start": v(35.54, 12.92) * mm, "mid": v(35.8, 13.06) * mm, "end": v(36.03, 13.24) * mm});
            skLineSegment(sketch, "E13.29.9", {"start": v(35.54, 12.92) * mm, "end": v(35.22, 12.8) * mm});
            skArc(sketch, "E13.30.0", {"start": v(33.18, 19.3) * mm, "mid": v(33.6, 19.92) * mm, "end": v(33.98, 20.58) * mm});
            skArc(sketch, "E13.30.1", {"start": v(33.98, 20.58) * mm, "mid": v(34.1, 21.09) * mm, "end": v(33.95, 21.58) * mm});
            skArc(sketch, "E13.30.2", {"start": v(33.9, 21.64) * mm, "mid": v(33.52, 22) * mm, "end": v(33.01, 22.1) * mm});
            skArc(sketch, "E13.30.3", {"start": v(31.51, 21.92) * mm, "mid": v(32.26, 22.04) * mm, "end": v(33.01, 22.1) * mm});
            skArc(sketch, "E13.30.4", {"start": v(28.55, 21.9) * mm, "mid": v(29.54, 21.3) * mm, "end": v(30.68, 21.52) * mm});
            skArc(sketch, "E13.30.5", {"start": v(32.47, 18.71) * mm, "mid": v(31.78, 17.78) * mm, "end": v(31.9, 16.62) * mm});
            skArc(sketch, "E13.30.6", {"start": v(31.51, 21.92) * mm, "mid": v(31.23, 21.84) * mm, "end": v(30.97, 21.7) * mm});
            skLineSegment(sketch, "E13.30.7", {"start": v(30.97, 21.7) * mm, "end": v(30.68, 21.52) * mm});
            skArc(sketch, "E13.30.8", {"start": v(32.76, 18.9) * mm, "mid": v(32.99, 19.08) * mm, "end": v(33.18, 19.3) * mm});
            skLineSegment(sketch, "E13.30.9", {"start": v(32.76, 18.9) * mm, "end": v(32.47, 18.71) * mm});
            skArc(sketch, "E13.31.0", {"start": v(29.33, 24.77) * mm, "mid": v(29.64, 25.46) * mm, "end": v(29.9, 26.17) * mm});
            skArc(sketch, "E13.31.1", {"start": v(29.9, 26.17) * mm, "mid": v(29.92, 26.69) * mm, "end": v(29.68, 27.15) * mm});
            skArc(sketch, "E13.31.2", {"start": v(29.63, 27.2) * mm, "mid": v(29.2, 27.48) * mm, "end": v(28.68, 27.5) * mm});
            skArc(sketch, "E13.31.3", {"start": v(27.23, 27.06) * mm, "mid": v(27.94, 27.3) * mm, "end": v(28.68, 27.5) * mm});
            skArc(sketch, "E13.31.4", {"start": v(24.32, 26.52) * mm, "mid": v(25.4, 26.1) * mm, "end": v(26.48, 26.52) * mm});
            skArc(sketch, "E13.31.5", {"start": v(28.72, 24.07) * mm, "mid": v(28.21, 23.03) * mm, "end": v(28.54, 21.91) * mm});
            skArc(sketch, "E13.31.6", {"start": v(27.23, 27.06) * mm, "mid": v(26.97, 26.93) * mm, "end": v(26.73, 26.75) * mm});
            skLineSegment(sketch, "E13.31.7", {"start": v(26.73, 26.75) * mm, "end": v(26.48, 26.52) * mm});
            skArc(sketch, "E13.31.8", {"start": v(28.98, 24.3) * mm, "mid": v(29.17, 24.52) * mm, "end": v(29.33, 24.77) * mm});
            skLineSegment(sketch, "E13.31.9", {"start": v(28.98, 24.3) * mm, "end": v(28.72, 24.07) * mm});
            skArc(sketch, "E13.32.0", {"start": v(24.58, 29.48) * mm, "mid": v(24.77, 30.22) * mm, "end": v(24.9, 30.96) * mm});
            skArc(sketch, "E13.32.1", {"start": v(24.9, 30.96) * mm, "mid": v(24.83, 31.48) * mm, "end": v(24.52, 31.89) * mm});
            skArc(sketch, "E13.32.2", {"start": v(24.46, 31.94) * mm, "mid": v(23.98, 32.13) * mm, "end": v(23.46, 32.06) * mm});
            skArc(sketch, "E13.32.3", {"start": v(22.12, 31.38) * mm, "mid": v(22.78, 31.74) * mm, "end": v(23.46, 32.06) * mm});
            skArc(sketch, "E13.32.4", {"start": v(19.34, 30.34) * mm, "mid": v(20.48, 30.11) * mm, "end": v(21.47, 30.71) * mm});
            skArc(sketch, "E13.32.5", {"start": v(24.1, 28.69) * mm, "mid": v(23.78, 27.58) * mm, "end": v(24.3, 26.54) * mm});
            skArc(sketch, "E13.32.6", {"start": v(22.12, 31.38) * mm, "mid": v(21.88, 31.2) * mm, "end": v(21.68, 30.98) * mm});
            skLineSegment(sketch, "E13.32.7", {"start": v(21.68, 30.98) * mm, "end": v(21.47, 30.71) * mm});
            skArc(sketch, "E13.32.8", {"start": v(24.32, 28.96) * mm, "mid": v(24.47, 29.2) * mm, "end": v(24.58, 29.48) * mm});
            skLineSegment(sketch, "E13.32.9", {"start": v(24.32, 28.96) * mm, "end": v(24.1, 28.69) * mm});
            skArc(sketch, "E13.33.0", {"start": v(19.09, 33.3) * mm, "mid": v(19.14, 34.06) * mm, "end": v(19.14, 34.82) * mm});
            skArc(sketch, "E13.33.1", {"start": v(19.14, 34.82) * mm, "mid": v(18.99, 35.3) * mm, "end": v(18.6, 35.66) * mm});
            skArc(sketch, "E13.33.2", {"start": v(18.54, 35.7) * mm, "mid": v(18.03, 35.8) * mm, "end": v(17.54, 35.65) * mm});
            skArc(sketch, "E13.33.3", {"start": v(16.33, 34.74) * mm, "mid": v(16.92, 35.22) * mm, "end": v(17.54, 35.65) * mm});
            skArc(sketch, "E13.33.4", {"start": v(13.78, 33.24) * mm, "mid": v(14.94, 33.2) * mm, "end": v(15.81, 33.97) * mm});
            skArc(sketch, "E13.33.5", {"start": v(18.76, 32.44) * mm, "mid": v(18.63, 31.29) * mm, "end": v(19.32, 30.35) * mm});
            skArc(sketch, "E13.33.6", {"start": v(16.33, 34.74) * mm, "mid": v(16.13, 34.53) * mm, "end": v(15.97, 34.28) * mm});
            skLineSegment(sketch, "E13.33.7", {"start": v(15.97, 34.28) * mm, "end": v(15.81, 33.97) * mm});
            skArc(sketch, "E13.33.8", {"start": v(18.92, 32.74) * mm, "mid": v(19.03, 33.02) * mm, "end": v(19.09, 33.3) * mm});
            skLineSegment(sketch, "E13.33.9", {"start": v(18.92, 32.74) * mm, "end": v(18.76, 32.44) * mm});
            skArc(sketch, "E13.34.0", {"start": v(13.02, 36.11) * mm, "mid": v(12.94, 36.87) * mm, "end": v(12.8, 37.6) * mm});
            skArc(sketch, "E13.34.1", {"start": v(12.8, 37.6) * mm, "mid": v(12.57, 38.07) * mm, "end": v(12.13, 38.35) * mm});
            skArc(sketch, "E13.34.2", {"start": v(12.06, 38.37) * mm, "mid": v(11.54, 38.4) * mm, "end": v(11.08, 38.15) * mm});
            skArc(sketch, "E13.34.3", {"start": v(10.05, 37.05) * mm, "mid": v(10.55, 37.62) * mm, "end": v(11.08, 38.15) * mm});
            skArc(sketch, "E13.34.4", {"start": v(7.8, 35.12) * mm, "mid": v(8.95, 35.3) * mm, "end": v(9.67, 36.2) * mm});
            skArc(sketch, "E13.34.5", {"start": v(12.84, 35.2) * mm, "mid": v(12.92, 34.05) * mm, "end": v(13.76, 33.25) * mm});
            skArc(sketch, "E13.34.6", {"start": v(10.05, 37.05) * mm, "mid": v(9.89, 36.8) * mm, "end": v(9.78, 36.53) * mm});
            skLineSegment(sketch, "E13.34.7", {"start": v(9.78, 36.53) * mm, "end": v(9.67, 36.2) * mm});
            skArc(sketch, "E13.34.8", {"start": v(12.95, 35.53) * mm, "mid": v(13, 35.82) * mm, "end": v(13.02, 36.11) * mm});
            skLineSegment(sketch, "E13.34.9", {"start": v(12.95, 35.53) * mm, "end": v(12.84, 35.2) * mm});
            skArc(sketch, "E13.35.0", {"start": v(6.55, 37.82) * mm, "mid": v(6.34, 38.55) * mm, "end": v(6.08, 39.26) * mm});
            skArc(sketch, "E13.35.1", {"start": v(6.08, 39.26) * mm, "mid": v(5.76, 39.67) * mm, "end": v(5.29, 39.88) * mm});
            skArc(sketch, "E13.35.2", {"start": v(5.21, 39.89) * mm, "mid": v(4.7, 39.81) * mm, "end": v(4.3, 39.5) * mm});
            skArc(sketch, "E13.35.3", {"start": v(3.46, 38.23) * mm, "mid": v(3.85, 38.88) * mm, "end": v(4.3, 39.5) * mm});
            skArc(sketch, "E13.35.4", {"start": v(1.58, 35.94) * mm, "mid": v(2.68, 36.32) * mm, "end": v(3.24, 37.33) * mm});
            skArc(sketch, "E13.35.5", {"start": v(6.53, 36.9) * mm, "mid": v(6.81, 35.77) * mm, "end": v(7.77, 35.13) * mm});
            skArc(sketch, "E13.35.6", {"start": v(3.46, 38.23) * mm, "mid": v(3.35, 37.96) * mm, "end": v(3.28, 37.67) * mm});
            skLineSegment(sketch, "E13.35.7", {"start": v(3.28, 37.67) * mm, "end": v(3.24, 37.33) * mm});
            skArc(sketch, "E13.35.8", {"start": v(6.58, 37.24) * mm, "mid": v(6.6, 37.53) * mm, "end": v(6.55, 37.82) * mm});
            skLineSegment(sketch, "E13.35.9", {"start": v(6.58, 37.24) * mm, "end": v(6.53, 36.9) * mm});
            skArc(sketch, "E14.trimOffspring", {"start": v(1.58, 35.94) * mm, "mid": v(1.57, 35.94) * mm, "end": v(1.56, 35.95) * mm});
            skArc(sketch, "E15.trimOffspring", {"start": v(7.8, 35.12) * mm, "mid": v(7.79, 35.13) * mm, "end": v(7.77, 35.13) * mm});
            skArc(sketch, "E16.trimOffspring", {"start": v(13.78, 33.24) * mm, "mid": v(13.77, 33.24) * mm, "end": v(13.76, 33.25) * mm});
            skArc(sketch, "E17.trimOffspring", {"start": v(19.34, 30.34) * mm, "mid": v(19.33, 30.34) * mm, "end": v(19.32, 30.35) * mm});
            skArc(sketch, "E18.trimOffspring", {"start": v(24.32, 26.52) * mm, "mid": v(24.3, 26.53) * mm, "end": v(24.3, 26.54) * mm});
            skArc(sketch, "E19.trimOffspring", {"start": v(28.55, 21.9) * mm, "mid": v(28.54, 21.9) * mm, "end": v(28.54, 21.91) * mm});
            skArc(sketch, "E20.trimOffspring", {"start": v(31.92, 16.6) * mm, "mid": v(31.91, 16.61) * mm, "end": v(31.9, 16.62) * mm});
            skArc(sketch, "E21.trimOffspring", {"start": v(34.32, 10.8) * mm, "mid": v(34.31, 10.82) * mm, "end": v(34.31, 10.83) * mm});
            skArc(sketch, "E22.trimOffspring", {"start": v(35.67, 4.68) * mm, "mid": v(35.67, 4.7) * mm, "end": v(35.67, 4.7) * mm});
            skArc(sketch, "E23.trimOffspring", {"start": v(-10.8, 34.32) * mm, "mid": v(-10.82, 34.31) * mm, "end": v(-10.83, 34.31) * mm});
            skArc(sketch, "E24.trimOffspring", {"start": v(-16.6, 31.92) * mm, "mid": v(-16.61, 31.91) * mm, "end": v(-16.62, 31.9) * mm});
            skArc(sketch, "E25.trimOffspring", {"start": v(-21.9, 28.55) * mm, "mid": v(-21.9, 28.54) * mm, "end": v(-21.91, 28.54) * mm});
            skArc(sketch, "E26.trimOffspring", {"start": v(-26.52, 24.32) * mm, "mid": v(-26.53, 24.3) * mm, "end": v(-26.54, 24.3) * mm});
            skArc(sketch, "E27.trimOffspring", {"start": v(-30.34, 19.34) * mm, "mid": v(-30.34, 19.33) * mm, "end": v(-30.35, 19.32) * mm});
            skArc(sketch, "E28.trimOffspring", {"start": v(-33.24, 13.78) * mm, "mid": v(-33.24, 13.77) * mm, "end": v(-33.25, 13.76) * mm});
            skArc(sketch, "E29.trimOffspring", {"start": v(-35.12, 7.8) * mm, "mid": v(-35.13, 7.79) * mm, "end": v(-35.13, 7.77) * mm});
            skArc(sketch, "E30.trimOffspring", {"start": v(-35.94, 1.58) * mm, "mid": v(-35.94, 1.57) * mm, "end": v(-35.95, 1.56) * mm});
            skArc(sketch, "E31.trimOffspring", {"start": v(-35.67, -4.68) * mm, "mid": v(-35.67, -4.7) * mm, "end": v(-35.67, -4.7) * mm});
            skArc(sketch, "E32.trimOffspring", {"start": v(-34.32, -10.8) * mm, "mid": v(-34.31, -10.82) * mm, "end": v(-34.31, -10.83) * mm});
            skArc(sketch, "E33.trimOffspring", {"start": v(-31.92, -16.6) * mm, "mid": v(-31.91, -16.61) * mm, "end": v(-31.9, -16.62) * mm});
            skArc(sketch, "E34.trimOffspring", {"start": v(35.94, -1.58) * mm, "mid": v(35.94, -1.57) * mm, "end": v(35.95, -1.56) * mm});
            skArc(sketch, "E35.trimOffspring", {"start": v(35.12, -7.8) * mm, "mid": v(35.13, -7.79) * mm, "end": v(35.13, -7.77) * mm});
            skArc(sketch, "E36.trimOffspring", {"start": v(33.24, -13.78) * mm, "mid": v(33.24, -13.77) * mm, "end": v(33.25, -13.76) * mm});
            skArc(sketch, "E37.trimOffspring", {"start": v(30.34, -19.34) * mm, "mid": v(30.34, -19.33) * mm, "end": v(30.35, -19.32) * mm});
            skArc(sketch, "E38.trimOffspring", {"start": v(-28.55, -21.9) * mm, "mid": v(-28.54, -21.9) * mm, "end": v(-28.54, -21.91) * mm});
            skArc(sketch, "E39.trimOffspring", {"start": v(-24.32, -26.52) * mm, "mid": v(-24.3, -26.53) * mm, "end": v(-24.3, -26.54) * mm});
            skArc(sketch, "E40.trimOffspring", {"start": v(-19.34, -30.34) * mm, "mid": v(-19.33, -30.34) * mm, "end": v(-19.32, -30.35) * mm});
            skArc(sketch, "E41.trimOffspring", {"start": v(-13.78, -33.24) * mm, "mid": v(-13.77, -33.24) * mm, "end": v(-13.76, -33.25) * mm});
            skArc(sketch, "E42.trimOffspring", {"start": v(-7.8, -35.12) * mm, "mid": v(-7.79, -35.13) * mm, "end": v(-7.77, -35.13) * mm});
            skArc(sketch, "E43.trimOffspring", {"start": v(-1.58, -35.94) * mm, "mid": v(-1.57, -35.94) * mm, "end": v(-1.56, -35.95) * mm});
            skArc(sketch, "E44.trimOffspring", {"start": v(4.68, -35.67) * mm, "mid": v(4.7, -35.67) * mm, "end": v(4.7, -35.67) * mm});
            skArc(sketch, "E45.trimOffspring", {"start": v(10.8, -34.32) * mm, "mid": v(10.82, -34.31) * mm, "end": v(10.83, -34.31) * mm});
            skArc(sketch, "E46.trimOffspring", {"start": v(16.6, -31.92) * mm, "mid": v(16.61, -31.91) * mm, "end": v(16.62, -31.9) * mm});
            skArc(sketch, "E47.trimOffspring", {"start": v(21.9, -28.55) * mm, "mid": v(21.9, -28.54) * mm, "end": v(21.91, -28.54) * mm});
            skArc(sketch, "E48.trimOffspring", {"start": v(26.52, -24.32) * mm, "mid": v(26.53, -24.3) * mm, "end": v(26.54, -24.3) * mm});
            skLineSegment(sketch, "E49", {"start": v(5.21, 39.89) * mm, "end": v(5.29, 39.88) * mm});
            skLineSegment(sketch, "E50", {"start": v(-8.67, 39.28) * mm, "end": v(-8.74, 39.26) * mm});
            skLineSegment(sketch, "E51", {"start": v(-15.36, 37.18) * mm, "end": v(-15.43, 37.15) * mm});
            skLineSegment(sketch, "E52", {"start": v(-21.64, 33.9) * mm, "end": v(-21.58, 33.95) * mm});
            skLineSegment(sketch, "E53", {"start": v(-27.15, 29.68) * mm, "end": v(-27.2, 29.63) * mm});
            skLineSegment(sketch, "E54", {"start": v(-31.89, 24.52) * mm, "end": v(-31.94, 24.46) * mm});
            skLineSegment(sketch, "E55", {"start": v(-35.66, 18.6) * mm, "end": v(-35.7, 18.54) * mm});
            skLineSegment(sketch, "E56", {"start": v(-38.35, 12.13) * mm, "end": v(-38.37, 12.06) * mm});
            skLineSegment(sketch, "E57", {"start": v(-39.88, 5.29) * mm, "end": v(-39.89, 5.21) * mm});
            skLineSegment(sketch, "E58", {"start": v(-40.19, -1.72) * mm, "end": v(-40.18, -1.8) * mm});
            skLineSegment(sketch, "E59", {"start": v(-39.28, -8.67) * mm, "end": v(-39.26, -8.74) * mm});
            skLineSegment(sketch, "E60", {"start": v(-37.18, -15.36) * mm, "end": v(-37.15, -15.43) * mm});
            skLineSegment(sketch, "E61", {"start": v(-33.95, -21.58) * mm, "end": v(-33.9, -21.64) * mm});
            skLineSegment(sketch, "E62", {"start": v(-29.68, -27.15) * mm, "end": v(-29.63, -27.2) * mm});
            skLineSegment(sketch, "E63", {"start": v(-24.46, -31.94) * mm, "end": v(-24.52, -31.89) * mm});
            skLineSegment(sketch, "E64", {"start": v(-18.6, -35.66) * mm, "end": v(-18.54, -35.7) * mm});
            skLineSegment(sketch, "E65", {"start": v(-12.13, -38.35) * mm, "end": v(-12.06, -38.37) * mm});
            skLineSegment(sketch, "E66", {"start": v(-5.29, -39.88) * mm, "end": v(-5.21, -39.89) * mm});
            skLineSegment(sketch, "E67", {"start": v(1.8, -40.18) * mm, "end": v(1.72, -40.19) * mm});
            skLineSegment(sketch, "E68", {"start": v(8.67, -39.28) * mm, "end": v(8.74, -39.26) * mm});
            skLineSegment(sketch, "E69", {"start": v(15.43, -37.15) * mm, "end": v(15.36, -37.18) * mm});
            skLineSegment(sketch, "E70", {"start": v(21.64, -33.9) * mm, "end": v(21.58, -33.95) * mm});
            skLineSegment(sketch, "E71", {"start": v(27.2, -29.63) * mm, "end": v(27.15, -29.68) * mm});
            skLineSegment(sketch, "E72", {"start": v(31.94, -24.46) * mm, "end": v(31.89, -24.52) * mm});
            skLineSegment(sketch, "E73", {"start": v(35.7, -18.54) * mm, "end": v(35.66, -18.6) * mm});
            skLineSegment(sketch, "E74", {"start": v(38.37, -12.06) * mm, "end": v(38.35, -12.13) * mm});
            skLineSegment(sketch, "E75", {"start": v(39.89, -5.21) * mm, "end": v(39.88, -5.29) * mm});
            skLineSegment(sketch, "E76", {"start": v(40.19, 1.72) * mm, "end": v(40.18, 1.8) * mm});
            skLineSegment(sketch, "E77", {"start": v(39.28, 8.67) * mm, "end": v(39.26, 8.74) * mm});
            skLineSegment(sketch, "E78", {"start": v(37.15, 15.43) * mm, "end": v(37.18, 15.36) * mm});
            skLineSegment(sketch, "E79", {"start": v(33.95, 21.58) * mm, "end": v(33.9, 21.64) * mm});
            skLineSegment(sketch, "E80", {"start": v(29.63, 27.2) * mm, "end": v(29.68, 27.15) * mm});
            skLineSegment(sketch, "E81", {"start": v(24.52, 31.89) * mm, "end": v(24.46, 31.94) * mm});
            skLineSegment(sketch, "E82", {"start": v(18.54, 35.7) * mm, "end": v(18.6, 35.66) * mm});
            skLineSegment(sketch, "E83", {"start": v(12.06, 38.37) * mm, "end": v(12.13, 38.35) * mm});
            skSolve(sketch);
        }
        {
            var Q0;
            Q0=makeQuery(id+"F0.imprint","IMPRINT",FACE,{"disambiguationData":[TD([[makeQuery(id+"F0.imprint","IMPRINT",EDGE,{"derivedFrom":sQuery(id+"F0.wireOp",EDGE,"E0")}),1.0]])]});
            extrude(context, id + "F1", {"entities" : qUnion([Q0]), "depth" : 6.35 * mm});
        }
        {
            var Q0;
            Q0=makeQuery(id+"F1.opExtrude","CAP_FACE",FACE,{"disambiguationData":[OSD([sQuery(id+"F0.wireOp",EDGE,"E0"),sQuery(id+"F0.wireOp",EDGE,"E1.trimOffspring"),sQuery(id+"F0.wireOp",EDGE,"E2"),sQuery(id+"F0.wireOp",EDGE,"E3"),sQuery(id+"F0.wireOp",EDGE,"E4.MirrorCS"),sQuery(id+"F0.wireOp",EDGE,"E5.MirrorCS"),sQuery(id+"F0.wireOp",EDGE,"E6.MirrorCS"),sQuery(id+"F0.wireOp",EDGE,"E7.filletArc"),sQuery(id+"F0.wireOp",EDGE,"E8.filletArc"),sQuery(id+"F0.wireOp",EDGE,"E9.filletArc"),sQuery(id+"F0.wireOp",EDGE,"E10.filletArc"),sQuery(id+"F0.wireOp",EDGE,"E11.filletArc"),sQuery(id+"F0.wireOp",EDGE,"E12.filletArc"),sQuery(id+"F0.wireOp",EDGE,"E13.1.0"),sQuery(id+"F0.wireOp",EDGE,"E13.1.1"),sQuery(id+"F0.wireOp",EDGE,"E13.1.2"),sQuery(id+"F0.wireOp",EDGE,"E13.1.3"),sQuery(id+"F0.wireOp",EDGE,"E13.1.4"),sQuery(id+"F0.wireOp",EDGE,"E13.1.5"),sQuery(id+"F0.wireOp",EDGE,"E13.1.6"),sQuery(id+"F0.wireOp",EDGE,"E13.1.7"),sQuery(id+"F0.wireOp",EDGE,"E13.1.8"),sQuery(id+"F0.wireOp",EDGE,"E13.1.9"),sQuery(id+"F0.wireOp",EDGE,"E13.2.0"),sQuery(id+"F0.wireOp",EDGE,"E13.2.1"),sQuery(id+"F0.wireOp",EDGE,"E13.2.2"),sQuery(id+"F0.wireOp",EDGE,"E13.2.3"),sQuery(id+"F0.wireOp",EDGE,"E13.2.4"),sQuery(id+"F0.wireOp",EDGE,"E13.2.5"),sQuery(id+"F0.wireOp",EDGE,"E13.2.6"),sQuery(id+"F0.wireOp",EDGE,"E13.2.7"),sQuery(id+"F0.wireOp",EDGE,"E13.2.8"),sQuery(id+"F0.wireOp",EDGE,"E13.2.9"),sQuery(id+"F0.wireOp",EDGE,"E13.3.0"),sQuery(id+"F0.wireOp",EDGE,"E13.3.1"),sQuery(id+"F0.wireOp",EDGE,"E13.3.2"),sQuery(id+"F0.wireOp",EDGE,"E13.3.3"),sQuery(id+"F0.wireOp",EDGE,"E13.3.4"),sQuery(id+"F0.wireOp",EDGE,"E13.3.5"),sQuery(id+"F0.wireOp",EDGE,"E13.3.6"),sQuery(id+"F0.wireOp",EDGE,"E13.3.7"),sQuery(id+"F0.wireOp",EDGE,"E13.3.8"),sQuery(id+"F0.wireOp",EDGE,"E13.3.9"),sQuery(id+"F0.wireOp",EDGE,"E13.4.0"),sQuery(id+"F0.wireOp",EDGE,"E13.4.1"),sQuery(id+"F0.wireOp",EDGE,"E13.4.2"),sQuery(id+"F0.wireOp",EDGE,"E13.4.3"),sQuery(id+"F0.wireOp",EDGE,"E13.4.4"),sQuery(id+"F0.wireOp",EDGE,"E13.4.5"),sQuery(id+"F0.wireOp",EDGE,"E13.4.6"),sQuery(id+"F0.wireOp",EDGE,"E13.4.7"),sQuery(id+"F0.wireOp",EDGE,"E13.4.8"),sQuery(id+"F0.wireOp",EDGE,"E13.4.9"),sQuery(id+"F0.wireOp",EDGE,"E13.5.0"),sQuery(id+"F0.wireOp",EDGE,"E13.5.1"),sQuery(id+"F0.wireOp",EDGE,"E13.5.2"),sQuery(id+"F0.wireOp",EDGE,"E13.5.3"),sQuery(id+"F0.wireOp",EDGE,"E13.5.4"),sQuery(id+"F0.wireOp",EDGE,"E13.5.5"),sQuery(id+"F0.wireOp",EDGE,"E13.5.6"),sQuery(id+"F0.wireOp",EDGE,"E13.5.7"),sQuery(id+"F0.wireOp",EDGE,"E13.5.8"),sQuery(id+"F0.wireOp",EDGE,"E13.5.9"),sQuery(id+"F0.wireOp",EDGE,"E13.6.0"),sQuery(id+"F0.wireOp",EDGE,"E13.6.1"),sQuery(id+"F0.wireOp",EDGE,"E13.6.2"),sQuery(id+"F0.wireOp",EDGE,"E13.6.3"),sQuery(id+"F0.wireOp",EDGE,"E13.6.4"),sQuery(id+"F0.wireOp",EDGE,"E13.6.5"),sQuery(id+"F0.wireOp",EDGE,"E13.6.6"),sQuery(id+"F0.wireOp",EDGE,"E13.6.7"),sQuery(id+"F0.wireOp",EDGE,"E13.6.8"),sQuery(id+"F0.wireOp",EDGE,"E13.6.9"),sQuery(id+"F0.wireOp",EDGE,"E13.7.0"),sQuery(id+"F0.wireOp",EDGE,"E13.7.1"),sQuery(id+"F0.wireOp",EDGE,"E13.7.2"),sQuery(id+"F0.wireOp",EDGE,"E13.7.3"),sQuery(id+"F0.wireOp",EDGE,"E13.7.4"),sQuery(id+"F0.wireOp",EDGE,"E13.7.5"),sQuery(id+"F0.wireOp",EDGE,"E13.7.6"),sQuery(id+"F0.wireOp",EDGE,"E13.7.7"),sQuery(id+"F0.wireOp",EDGE,"E13.7.8"),sQuery(id+"F0.wireOp",EDGE,"E13.7.9"),sQuery(id+"F0.wireOp",EDGE,"E13.8.0"),sQuery(id+"F0.wireOp",EDGE,"E13.8.1"),sQuery(id+"F0.wireOp",EDGE,"E13.8.2"),sQuery(id+"F0.wireOp",EDGE,"E13.8.3"),sQuery(id+"F0.wireOp",EDGE,"E13.8.4"),sQuery(id+"F0.wireOp",EDGE,"E13.8.5"),sQuery(id+"F0.wireOp",EDGE,"E13.8.6"),sQuery(id+"F0.wireOp",EDGE,"E13.8.7"),sQuery(id+"F0.wireOp",EDGE,"E13.8.8"),sQuery(id+"F0.wireOp",EDGE,"E13.8.9"),sQuery(id+"F0.wireOp",EDGE,"E13.9.0"),sQuery(id+"F0.wireOp",EDGE,"E13.9.1"),sQuery(id+"F0.wireOp",EDGE,"E13.9.2"),sQuery(id+"F0.wireOp",EDGE,"E13.9.3"),sQuery(id+"F0.wireOp",EDGE,"E13.9.4"),sQuery(id+"F0.wireOp",EDGE,"E13.9.5"),sQuery(id+"F0.wireOp",EDGE,"E13.9.6"),sQuery(id+"F0.wireOp",EDGE,"E13.9.7"),sQuery(id+"F0.wireOp",EDGE,"E13.9.8"),sQuery(id+"F0.wireOp",EDGE,"E13.9.9"),sQuery(id+"F0.wireOp",EDGE,"E13.10.0"),sQuery(id+"F0.wireOp",EDGE,"E13.10.1"),sQuery(id+"F0.wireOp",EDGE,"E13.10.2"),sQuery(id+"F0.wireOp",EDGE,"E13.10.3"),sQuery(id+"F0.wireOp",EDGE,"E13.10.4"),sQuery(id+"F0.wireOp",EDGE,"E13.10.5"),sQuery(id+"F0.wireOp",EDGE,"E13.10.6"),sQuery(id+"F0.wireOp",EDGE,"E13.10.7"),sQuery(id+"F0.wireOp",EDGE,"E13.10.8"),sQuery(id+"F0.wireOp",EDGE,"E13.10.9"),sQuery(id+"F0.wireOp",EDGE,"E13.11.0"),sQuery(id+"F0.wireOp",EDGE,"E13.11.1"),sQuery(id+"F0.wireOp",EDGE,"E13.11.2"),sQuery(id+"F0.wireOp",EDGE,"E13.11.3"),sQuery(id+"F0.wireOp",EDGE,"E13.11.4"),sQuery(id+"F0.wireOp",EDGE,"E13.11.5"),sQuery(id+"F0.wireOp",EDGE,"E13.11.6"),sQuery(id+"F0.wireOp",EDGE,"E13.11.7"),sQuery(id+"F0.wireOp",EDGE,"E13.11.8"),sQuery(id+"F0.wireOp",EDGE,"E13.11.9"),sQuery(id+"F0.wireOp",EDGE,"E13.12.0"),sQuery(id+"F0.wireOp",EDGE,"E13.12.1"),sQuery(id+"F0.wireOp",EDGE,"E13.12.2"),sQuery(id+"F0.wireOp",EDGE,"E13.12.3"),sQuery(id+"F0.wireOp",EDGE,"E13.12.4"),sQuery(id+"F0.wireOp",EDGE,"E13.12.5"),sQuery(id+"F0.wireOp",EDGE,"E13.12.6"),sQuery(id+"F0.wireOp",EDGE,"E13.12.7"),sQuery(id+"F0.wireOp",EDGE,"E13.12.8"),sQuery(id+"F0.wireOp",EDGE,"E13.12.9"),sQuery(id+"F0.wireOp",EDGE,"E13.13.0"),sQuery(id+"F0.wireOp",EDGE,"E13.13.1"),sQuery(id+"F0.wireOp",EDGE,"E13.13.2"),sQuery(id+"F0.wireOp",EDGE,"E13.13.3"),sQuery(id+"F0.wireOp",EDGE,"E13.13.4"),sQuery(id+"F0.wireOp",EDGE,"E13.13.5"),sQuery(id+"F0.wireOp",EDGE,"E13.13.6"),sQuery(id+"F0.wireOp",EDGE,"E13.13.7"),sQuery(id+"F0.wireOp",EDGE,"E13.13.8"),sQuery(id+"F0.wireOp",EDGE,"E13.13.9"),sQuery(id+"F0.wireOp",EDGE,"E13.14.0"),sQuery(id+"F0.wireOp",EDGE,"E13.14.1"),sQuery(id+"F0.wireOp",EDGE,"E13.14.2"),sQuery(id+"F0.wireOp",EDGE,"E13.14.3"),sQuery(id+"F0.wireOp",EDGE,"E13.14.4"),sQuery(id+"F0.wireOp",EDGE,"E13.14.5"),sQuery(id+"F0.wireOp",EDGE,"E13.14.6"),sQuery(id+"F0.wireOp",EDGE,"E13.14.7"),sQuery(id+"F0.wireOp",EDGE,"E13.14.8"),sQuery(id+"F0.wireOp",EDGE,"E13.14.9"),sQuery(id+"F0.wireOp",EDGE,"E13.15.0"),sQuery(id+"F0.wireOp",EDGE,"E13.15.1"),sQuery(id+"F0.wireOp",EDGE,"E13.15.2"),sQuery(id+"F0.wireOp",EDGE,"E13.15.3"),sQuery(id+"F0.wireOp",EDGE,"E13.15.4"),sQuery(id+"F0.wireOp",EDGE,"E13.15.5"),sQuery(id+"F0.wireOp",EDGE,"E13.15.6"),sQuery(id+"F0.wireOp",EDGE,"E13.15.7"),sQuery(id+"F0.wireOp",EDGE,"E13.15.8"),sQuery(id+"F0.wireOp",EDGE,"E13.15.9"),sQuery(id+"F0.wireOp",EDGE,"E13.16.0"),sQuery(id+"F0.wireOp",EDGE,"E13.16.1"),sQuery(id+"F0.wireOp",EDGE,"E13.16.2"),sQuery(id+"F0.wireOp",EDGE,"E13.16.3"),sQuery(id+"F0.wireOp",EDGE,"E13.16.4"),sQuery(id+"F0.wireOp",EDGE,"E13.16.5"),sQuery(id+"F0.wireOp",EDGE,"E13.16.6"),sQuery(id+"F0.wireOp",EDGE,"E13.16.7"),sQuery(id+"F0.wireOp",EDGE,"E13.16.8"),sQuery(id+"F0.wireOp",EDGE,"E13.16.9"),sQuery(id+"F0.wireOp",EDGE,"E13.17.0"),sQuery(id+"F0.wireOp",EDGE,"E13.17.1"),sQuery(id+"F0.wireOp",EDGE,"E13.17.2"),sQuery(id+"F0.wireOp",EDGE,"E13.17.3"),sQuery(id+"F0.wireOp",EDGE,"E13.17.4"),sQuery(id+"F0.wireOp",EDGE,"E13.17.5"),sQuery(id+"F0.wireOp",EDGE,"E13.17.6"),sQuery(id+"F0.wireOp",EDGE,"E13.17.7"),sQuery(id+"F0.wireOp",EDGE,"E13.17.8"),sQuery(id+"F0.wireOp",EDGE,"E13.17.9"),sQuery(id+"F0.wireOp",EDGE,"E13.18.0"),sQuery(id+"F0.wireOp",EDGE,"E13.18.1"),sQuery(id+"F0.wireOp",EDGE,"E13.18.2"),sQuery(id+"F0.wireOp",EDGE,"E13.18.3"),sQuery(id+"F0.wireOp",EDGE,"E13.18.4"),sQuery(id+"F0.wireOp",EDGE,"E13.18.5"),sQuery(id+"F0.wireOp",EDGE,"E13.18.6"),sQuery(id+"F0.wireOp",EDGE,"E13.18.7"),sQuery(id+"F0.wireOp",EDGE,"E13.18.8"),sQuery(id+"F0.wireOp",EDGE,"E13.18.9"),sQuery(id+"F0.wireOp",EDGE,"E13.19.0"),sQuery(id+"F0.wireOp",EDGE,"E13.19.1"),sQuery(id+"F0.wireOp",EDGE,"E13.19.2"),sQuery(id+"F0.wireOp",EDGE,"E13.19.3"),sQuery(id+"F0.wireOp",EDGE,"E13.19.4"),sQuery(id+"F0.wireOp",EDGE,"E13.19.5"),sQuery(id+"F0.wireOp",EDGE,"E13.19.6"),sQuery(id+"F0.wireOp",EDGE,"E13.19.7"),sQuery(id+"F0.wireOp",EDGE,"E13.19.8"),sQuery(id+"F0.wireOp",EDGE,"E13.19.9"),sQuery(id+"F0.wireOp",EDGE,"E13.20.0"),sQuery(id+"F0.wireOp",EDGE,"E13.20.1"),sQuery(id+"F0.wireOp",EDGE,"E13.20.2"),sQuery(id+"F0.wireOp",EDGE,"E13.20.3"),sQuery(id+"F0.wireOp",EDGE,"E13.20.4"),sQuery(id+"F0.wireOp",EDGE,"E13.20.5"),sQuery(id+"F0.wireOp",EDGE,"E13.20.6"),sQuery(id+"F0.wireOp",EDGE,"E13.20.7"),sQuery(id+"F0.wireOp",EDGE,"E13.20.8"),sQuery(id+"F0.wireOp",EDGE,"E13.20.9"),sQuery(id+"F0.wireOp",EDGE,"E13.21.0"),sQuery(id+"F0.wireOp",EDGE,"E13.21.1"),sQuery(id+"F0.wireOp",EDGE,"E13.21.2"),sQuery(id+"F0.wireOp",EDGE,"E13.21.3"),sQuery(id+"F0.wireOp",EDGE,"E13.21.4"),sQuery(id+"F0.wireOp",EDGE,"E13.21.5"),sQuery(id+"F0.wireOp",EDGE,"E13.21.6"),sQuery(id+"F0.wireOp",EDGE,"E13.21.7"),sQuery(id+"F0.wireOp",EDGE,"E13.21.8"),sQuery(id+"F0.wireOp",EDGE,"E13.21.9"),sQuery(id+"F0.wireOp",EDGE,"E13.22.0"),sQuery(id+"F0.wireOp",EDGE,"E13.22.1"),sQuery(id+"F0.wireOp",EDGE,"E13.22.2"),sQuery(id+"F0.wireOp",EDGE,"E13.22.3"),sQuery(id+"F0.wireOp",EDGE,"E13.22.4"),sQuery(id+"F0.wireOp",EDGE,"E13.22.5"),sQuery(id+"F0.wireOp",EDGE,"E13.22.6"),sQuery(id+"F0.wireOp",EDGE,"E13.22.7"),sQuery(id+"F0.wireOp",EDGE,"E13.22.8"),sQuery(id+"F0.wireOp",EDGE,"E13.22.9"),sQuery(id+"F0.wireOp",EDGE,"E13.23.0"),sQuery(id+"F0.wireOp",EDGE,"E13.23.1"),sQuery(id+"F0.wireOp",EDGE,"E13.23.2"),sQuery(id+"F0.wireOp",EDGE,"E13.23.3"),sQuery(id+"F0.wireOp",EDGE,"E13.23.4"),sQuery(id+"F0.wireOp",EDGE,"E13.23.5"),sQuery(id+"F0.wireOp",EDGE,"E13.23.6"),sQuery(id+"F0.wireOp",EDGE,"E13.23.7"),sQuery(id+"F0.wireOp",EDGE,"E13.23.8"),sQuery(id+"F0.wireOp",EDGE,"E13.23.9"),sQuery(id+"F0.wireOp",EDGE,"E13.24.0"),sQuery(id+"F0.wireOp",EDGE,"E13.24.1"),sQuery(id+"F0.wireOp",EDGE,"E13.24.2"),sQuery(id+"F0.wireOp",EDGE,"E13.24.3"),sQuery(id+"F0.wireOp",EDGE,"E13.24.4"),sQuery(id+"F0.wireOp",EDGE,"E13.24.5"),sQuery(id+"F0.wireOp",EDGE,"E13.24.6"),sQuery(id+"F0.wireOp",EDGE,"E13.24.7"),sQuery(id+"F0.wireOp",EDGE,"E13.24.8"),sQuery(id+"F0.wireOp",EDGE,"E13.24.9"),sQuery(id+"F0.wireOp",EDGE,"E13.25.0"),sQuery(id+"F0.wireOp",EDGE,"E13.25.1"),sQuery(id+"F0.wireOp",EDGE,"E13.25.2"),sQuery(id+"F0.wireOp",EDGE,"E13.25.3"),sQuery(id+"F0.wireOp",EDGE,"E13.25.4"),sQuery(id+"F0.wireOp",EDGE,"E13.25.5"),sQuery(id+"F0.wireOp",EDGE,"E13.25.6"),sQuery(id+"F0.wireOp",EDGE,"E13.25.7"),sQuery(id+"F0.wireOp",EDGE,"E13.25.8"),sQuery(id+"F0.wireOp",EDGE,"E13.25.9"),sQuery(id+"F0.wireOp",EDGE,"E13.26.0"),sQuery(id+"F0.wireOp",EDGE,"E13.26.1"),sQuery(id+"F0.wireOp",EDGE,"E13.26.2"),sQuery(id+"F0.wireOp",EDGE,"E13.26.3"),sQuery(id+"F0.wireOp",EDGE,"E13.26.4"),sQuery(id+"F0.wireOp",EDGE,"E13.26.5"),sQuery(id+"F0.wireOp",EDGE,"E13.26.6"),sQuery(id+"F0.wireOp",EDGE,"E13.26.7"),sQuery(id+"F0.wireOp",EDGE,"E13.26.8"),sQuery(id+"F0.wireOp",EDGE,"E13.26.9"),sQuery(id+"F0.wireOp",EDGE,"E13.27.0"),sQuery(id+"F0.wireOp",EDGE,"E13.27.1"),sQuery(id+"F0.wireOp",EDGE,"E13.27.2"),sQuery(id+"F0.wireOp",EDGE,"E13.27.3"),sQuery(id+"F0.wireOp",EDGE,"E13.27.4"),sQuery(id+"F0.wireOp",EDGE,"E13.27.5"),sQuery(id+"F0.wireOp",EDGE,"E13.27.6"),sQuery(id+"F0.wireOp",EDGE,"E13.27.7"),sQuery(id+"F0.wireOp",EDGE,"E13.27.8"),sQuery(id+"F0.wireOp",EDGE,"E13.27.9"),sQuery(id+"F0.wireOp",EDGE,"E13.28.0"),sQuery(id+"F0.wireOp",EDGE,"E13.28.1"),sQuery(id+"F0.wireOp",EDGE,"E13.28.2"),sQuery(id+"F0.wireOp",EDGE,"E13.28.3"),sQuery(id+"F0.wireOp",EDGE,"E13.28.4"),sQuery(id+"F0.wireOp",EDGE,"E13.28.5"),sQuery(id+"F0.wireOp",EDGE,"E13.28.6"),sQuery(id+"F0.wireOp",EDGE,"E13.28.7"),sQuery(id+"F0.wireOp",EDGE,"E13.28.8"),sQuery(id+"F0.wireOp",EDGE,"E13.28.9"),sQuery(id+"F0.wireOp",EDGE,"E13.29.0"),sQuery(id+"F0.wireOp",EDGE,"E13.29.1"),sQuery(id+"F0.wireOp",EDGE,"E13.29.2"),sQuery(id+"F0.wireOp",EDGE,"E13.29.3"),sQuery(id+"F0.wireOp",EDGE,"E13.29.4"),sQuery(id+"F0.wireOp",EDGE,"E13.29.5"),sQuery(id+"F0.wireOp",EDGE,"E13.29.6"),sQuery(id+"F0.wireOp",EDGE,"E13.29.7"),sQuery(id+"F0.wireOp",EDGE,"E13.29.8"),sQuery(id+"F0.wireOp",EDGE,"E13.29.9"),sQuery(id+"F0.wireOp",EDGE,"E13.30.0"),sQuery(id+"F0.wireOp",EDGE,"E13.30.1"),sQuery(id+"F0.wireOp",EDGE,"E13.30.2"),sQuery(id+"F0.wireOp",EDGE,"E13.30.3"),sQuery(id+"F0.wireOp",EDGE,"E13.30.4"),sQuery(id+"F0.wireOp",EDGE,"E13.30.5"),sQuery(id+"F0.wireOp",EDGE,"E13.30.6"),sQuery(id+"F0.wireOp",EDGE,"E13.30.7"),sQuery(id+"F0.wireOp",EDGE,"E13.30.8"),sQuery(id+"F0.wireOp",EDGE,"E13.30.9"),sQuery(id+"F0.wireOp",EDGE,"E13.31.0"),sQuery(id+"F0.wireOp",EDGE,"E13.31.1"),sQuery(id+"F0.wireOp",EDGE,"E13.31.2"),sQuery(id+"F0.wireOp",EDGE,"E13.31.3"),sQuery(id+"F0.wireOp",EDGE,"E13.31.4"),sQuery(id+"F0.wireOp",EDGE,"E13.31.5"),sQuery(id+"F0.wireOp",EDGE,"E13.31.6"),sQuery(id+"F0.wireOp",EDGE,"E13.31.7"),sQuery(id+"F0.wireOp",EDGE,"E13.31.8"),sQuery(id+"F0.wireOp",EDGE,"E13.31.9"),sQuery(id+"F0.wireOp",EDGE,"E13.32.0"),sQuery(id+"F0.wireOp",EDGE,"E13.32.1"),sQuery(id+"F0.wireOp",EDGE,"E13.32.2"),sQuery(id+"F0.wireOp",EDGE,"E13.32.3"),sQuery(id+"F0.wireOp",EDGE,"E13.32.4"),sQuery(id+"F0.wireOp",EDGE,"E13.32.5"),sQuery(id+"F0.wireOp",EDGE,"E13.32.6"),sQuery(id+"F0.wireOp",EDGE,"E13.32.7"),sQuery(id+"F0.wireOp",EDGE,"E13.32.8"),sQuery(id+"F0.wireOp",EDGE,"E13.32.9"),sQuery(id+"F0.wireOp",EDGE,"E13.33.0"),sQuery(id+"F0.wireOp",EDGE,"E13.33.1"),sQuery(id+"F0.wireOp",EDGE,"E13.33.2"),sQuery(id+"F0.wireOp",EDGE,"E13.33.3"),sQuery(id+"F0.wireOp",EDGE,"E13.33.4"),sQuery(id+"F0.wireOp",EDGE,"E13.33.5"),sQuery(id+"F0.wireOp",EDGE,"E13.33.6"),sQuery(id+"F0.wireOp",EDGE,"E13.33.7"),sQuery(id+"F0.wireOp",EDGE,"E13.33.8"),sQuery(id+"F0.wireOp",EDGE,"E13.33.9"),sQuery(id+"F0.wireOp",EDGE,"E13.34.0"),sQuery(id+"F0.wireOp",EDGE,"E13.34.1"),sQuery(id+"F0.wireOp",EDGE,"E13.34.2"),sQuery(id+"F0.wireOp",EDGE,"E13.34.3"),sQuery(id+"F0.wireOp",EDGE,"E13.34.4"),sQuery(id+"F0.wireOp",EDGE,"E13.34.5"),sQuery(id+"F0.wireOp",EDGE,"E13.34.6"),sQuery(id+"F0.wireOp",EDGE,"E13.34.7"),sQuery(id+"F0.wireOp",EDGE,"E13.34.8"),sQuery(id+"F0.wireOp",EDGE,"E13.34.9"),sQuery(id+"F0.wireOp",EDGE,"E13.35.0"),sQuery(id+"F0.wireOp",EDGE,"E13.35.1"),sQuery(id+"F0.wireOp",EDGE,"E13.35.2"),sQuery(id+"F0.wireOp",EDGE,"E13.35.3"),sQuery(id+"F0.wireOp",EDGE,"E13.35.4"),sQuery(id+"F0.wireOp",EDGE,"E13.35.5"),sQuery(id+"F0.wireOp",EDGE,"E13.35.6"),sQuery(id+"F0.wireOp",EDGE,"E13.35.7"),sQuery(id+"F0.wireOp",EDGE,"E13.35.8"),sQuery(id+"F0.wireOp",EDGE,"E13.35.9"),sQuery(id+"F0.wireOp",EDGE,"E14.trimOffspring"),sQuery(id+"F0.wireOp",EDGE,"E15.trimOffspring"),sQuery(id+"F0.wireOp",EDGE,"E16.trimOffspring"),sQuery(id+"F0.wireOp",EDGE,"E17.trimOffspring"),sQuery(id+"F0.wireOp",EDGE,"E18.trimOffspring"),sQuery(id+"F0.wireOp",EDGE,"E19.trimOffspring"),sQuery(id+"F0.wireOp",EDGE,"E20.trimOffspring"),sQuery(id+"F0.wireOp",EDGE,"E21.trimOffspring"),sQuery(id+"F0.wireOp",EDGE,"E22.trimOffspring"),sQuery(id+"F0.wireOp",EDGE,"E23.trimOffspring"),sQuery(id+"F0.wireOp",EDGE,"E24.trimOffspring"),sQuery(id+"F0.wireOp",EDGE,"E25.trimOffspring"),sQuery(id+"F0.wireOp",EDGE,"E26.trimOffspring"),sQuery(id+"F0.wireOp",EDGE,"E27.trimOffspring"),sQuery(id+"F0.wireOp",EDGE,"E28.trimOffspring"),sQuery(id+"F0.wireOp",EDGE,"E29.trimOffspring"),sQuery(id+"F0.wireOp",EDGE,"E30.trimOffspring"),sQuery(id+"F0.wireOp",EDGE,"E31.trimOffspring"),sQuery(id+"F0.wireOp",EDGE,"E32.trimOffspring"),sQuery(id+"F0.wireOp",EDGE,"E33.trimOffspring"),sQuery(id+"F0.wireOp",EDGE,"E34.trimOffspring"),sQuery(id+"F0.wireOp",EDGE,"E35.trimOffspring"),sQuery(id+"F0.wireOp",EDGE,"E36.trimOffspring"),sQuery(id+"F0.wireOp",EDGE,"E37.trimOffspring"),sQuery(id+"F0.wireOp",EDGE,"E38.trimOffspring"),sQuery(id+"F0.wireOp",EDGE,"E39.trimOffspring"),sQuery(id+"F0.wireOp",EDGE,"E40.trimOffspring"),sQuery(id+"F0.wireOp",EDGE,"E41.trimOffspring"),sQuery(id+"F0.wireOp",EDGE,"E42.trimOffspring"),sQuery(id+"F0.wireOp",EDGE,"E43.trimOffspring"),sQuery(id+"F0.wireOp",EDGE,"E44.trimOffspring"),sQuery(id+"F0.wireOp",EDGE,"E45.trimOffspring"),sQuery(id+"F0.wireOp",EDGE,"E46.trimOffspring"),sQuery(id+"F0.wireOp",EDGE,"E47.trimOffspring"),sQuery(id+"F0.wireOp",EDGE,"E48.trimOffspring"),sQuery(id+"F0.wireOp",EDGE,"E49"),sQuery(id+"F0.wireOp",EDGE,"E50"),sQuery(id+"F0.wireOp",EDGE,"E51"),sQuery(id+"F0.wireOp",EDGE,"E52"),sQuery(id+"F0.wireOp",EDGE,"E53"),sQuery(id+"F0.wireOp",EDGE,"E54"),sQuery(id+"F0.wireOp",EDGE,"E55"),sQuery(id+"F0.wireOp",EDGE,"E56"),sQuery(id+"F0.wireOp",EDGE,"E57"),sQuery(id+"F0.wireOp",EDGE,"E58"),sQuery(id+"F0.wireOp",EDGE,"E59"),sQuery(id+"F0.wireOp",EDGE,"E60"),sQuery(id+"F0.wireOp",EDGE,"E61"),sQuery(id+"F0.wireOp",EDGE,"E62"),sQuery(id+"F0.wireOp",EDGE,"E63"),sQuery(id+"F0.wireOp",EDGE,"E64"),sQuery(id+"F0.wireOp",EDGE,"E65"),sQuery(id+"F0.wireOp",EDGE,"E66"),sQuery(id+"F0.wireOp",EDGE,"E67"),sQuery(id+"F0.wireOp",EDGE,"E68"),sQuery(id+"F0.wireOp",EDGE,"E69"),sQuery(id+"F0.wireOp",EDGE,"E70"),sQuery(id+"F0.wireOp",EDGE,"E71"),sQuery(id+"F0.wireOp",EDGE,"E72"),sQuery(id+"F0.wireOp",EDGE,"E73"),sQuery(id+"F0.wireOp",EDGE,"E74"),sQuery(id+"F0.wireOp",EDGE,"E75"),sQuery(id+"F0.wireOp",EDGE,"E76"),sQuery(id+"F0.wireOp",EDGE,"E77"),sQuery(id+"F0.wireOp",EDGE,"E78"),sQuery(id+"F0.wireOp",EDGE,"E79"),sQuery(id+"F0.wireOp",EDGE,"E80"),sQuery(id+"F0.wireOp",EDGE,"E81"),sQuery(id+"F0.wireOp",EDGE,"E82"),sQuery(id+"F0.wireOp",EDGE,"E83")])],"isStart":false});
            var sketch = newSketch(context, id + "F2", { "sketchPlane" : qUnion([Q0])});
            skPoint(sketch, "E84", {"position": v(0, 0) * mm});
            skSolve(sketch);
        }
        {
            var Q0;
            Q0=sQuery(id+"F2.wireOp",VERTEX,"E84");
            var Q1;
            Q1=makeQuery(id+"F1.opExtrude","SWEPT_BODY",BODY,{"disambiguationData":[OSD([sQuery(id+"F0.wireOp",EDGE,"E0"),sQuery(id+"F0.wireOp",EDGE,"E1.trimOffspring"),sQuery(id+"F0.wireOp",EDGE,"E2"),sQuery(id+"F0.wireOp",EDGE,"E3"),sQuery(id+"F0.wireOp",EDGE,"E4.MirrorCS"),sQuery(id+"F0.wireOp",EDGE,"E5.MirrorCS"),sQuery(id+"F0.wireOp",EDGE,"E6.MirrorCS"),sQuery(id+"F0.wireOp",EDGE,"E7.filletArc"),sQuery(id+"F0.wireOp",EDGE,"E8.filletArc"),sQuery(id+"F0.wireOp",EDGE,"E9.filletArc"),sQuery(id+"F0.wireOp",EDGE,"E10.filletArc"),sQuery(id+"F0.wireOp",EDGE,"E11.filletArc"),sQuery(id+"F0.wireOp",EDGE,"E12.filletArc"),sQuery(id+"F0.wireOp",EDGE,"E13.1.0"),sQuery(id+"F0.wireOp",EDGE,"E13.1.1"),sQuery(id+"F0.wireOp",EDGE,"E13.1.2"),sQuery(id+"F0.wireOp",EDGE,"E13.1.3"),sQuery(id+"F0.wireOp",EDGE,"E13.1.4"),sQuery(id+"F0.wireOp",EDGE,"E13.1.5"),sQuery(id+"F0.wireOp",EDGE,"E13.1.6"),sQuery(id+"F0.wireOp",EDGE,"E13.1.7"),sQuery(id+"F0.wireOp",EDGE,"E13.1.8"),sQuery(id+"F0.wireOp",EDGE,"E13.1.9"),sQuery(id+"F0.wireOp",EDGE,"E13.2.0"),sQuery(id+"F0.wireOp",EDGE,"E13.2.1"),sQuery(id+"F0.wireOp",EDGE,"E13.2.2"),sQuery(id+"F0.wireOp",EDGE,"E13.2.3"),sQuery(id+"F0.wireOp",EDGE,"E13.2.4"),sQuery(id+"F0.wireOp",EDGE,"E13.2.5"),sQuery(id+"F0.wireOp",EDGE,"E13.2.6"),sQuery(id+"F0.wireOp",EDGE,"E13.2.7"),sQuery(id+"F0.wireOp",EDGE,"E13.2.8"),sQuery(id+"F0.wireOp",EDGE,"E13.2.9"),sQuery(id+"F0.wireOp",EDGE,"E13.3.0"),sQuery(id+"F0.wireOp",EDGE,"E13.3.1"),sQuery(id+"F0.wireOp",EDGE,"E13.3.2"),sQuery(id+"F0.wireOp",EDGE,"E13.3.3"),sQuery(id+"F0.wireOp",EDGE,"E13.3.4"),sQuery(id+"F0.wireOp",EDGE,"E13.3.5"),sQuery(id+"F0.wireOp",EDGE,"E13.3.6"),sQuery(id+"F0.wireOp",EDGE,"E13.3.7"),sQuery(id+"F0.wireOp",EDGE,"E13.3.8"),sQuery(id+"F0.wireOp",EDGE,"E13.3.9"),sQuery(id+"F0.wireOp",EDGE,"E13.4.0"),sQuery(id+"F0.wireOp",EDGE,"E13.4.1"),sQuery(id+"F0.wireOp",EDGE,"E13.4.2"),sQuery(id+"F0.wireOp",EDGE,"E13.4.3"),sQuery(id+"F0.wireOp",EDGE,"E13.4.4"),sQuery(id+"F0.wireOp",EDGE,"E13.4.5"),sQuery(id+"F0.wireOp",EDGE,"E13.4.6"),sQuery(id+"F0.wireOp",EDGE,"E13.4.7"),sQuery(id+"F0.wireOp",EDGE,"E13.4.8"),sQuery(id+"F0.wireOp",EDGE,"E13.4.9"),sQuery(id+"F0.wireOp",EDGE,"E13.5.0"),sQuery(id+"F0.wireOp",EDGE,"E13.5.1"),sQuery(id+"F0.wireOp",EDGE,"E13.5.2"),sQuery(id+"F0.wireOp",EDGE,"E13.5.3"),sQuery(id+"F0.wireOp",EDGE,"E13.5.4"),sQuery(id+"F0.wireOp",EDGE,"E13.5.5"),sQuery(id+"F0.wireOp",EDGE,"E13.5.6"),sQuery(id+"F0.wireOp",EDGE,"E13.5.7"),sQuery(id+"F0.wireOp",EDGE,"E13.5.8"),sQuery(id+"F0.wireOp",EDGE,"E13.5.9"),sQuery(id+"F0.wireOp",EDGE,"E13.6.0"),sQuery(id+"F0.wireOp",EDGE,"E13.6.1"),sQuery(id+"F0.wireOp",EDGE,"E13.6.2"),sQuery(id+"F0.wireOp",EDGE,"E13.6.3"),sQuery(id+"F0.wireOp",EDGE,"E13.6.4"),sQuery(id+"F0.wireOp",EDGE,"E13.6.5"),sQuery(id+"F0.wireOp",EDGE,"E13.6.6"),sQuery(id+"F0.wireOp",EDGE,"E13.6.7"),sQuery(id+"F0.wireOp",EDGE,"E13.6.8"),sQuery(id+"F0.wireOp",EDGE,"E13.6.9"),sQuery(id+"F0.wireOp",EDGE,"E13.7.0"),sQuery(id+"F0.wireOp",EDGE,"E13.7.1"),sQuery(id+"F0.wireOp",EDGE,"E13.7.2"),sQuery(id+"F0.wireOp",EDGE,"E13.7.3"),sQuery(id+"F0.wireOp",EDGE,"E13.7.4"),sQuery(id+"F0.wireOp",EDGE,"E13.7.5"),sQuery(id+"F0.wireOp",EDGE,"E13.7.6"),sQuery(id+"F0.wireOp",EDGE,"E13.7.7"),sQuery(id+"F0.wireOp",EDGE,"E13.7.8"),sQuery(id+"F0.wireOp",EDGE,"E13.7.9"),sQuery(id+"F0.wireOp",EDGE,"E13.8.0"),sQuery(id+"F0.wireOp",EDGE,"E13.8.1"),sQuery(id+"F0.wireOp",EDGE,"E13.8.2"),sQuery(id+"F0.wireOp",EDGE,"E13.8.3"),sQuery(id+"F0.wireOp",EDGE,"E13.8.4"),sQuery(id+"F0.wireOp",EDGE,"E13.8.5"),sQuery(id+"F0.wireOp",EDGE,"E13.8.6"),sQuery(id+"F0.wireOp",EDGE,"E13.8.7"),sQuery(id+"F0.wireOp",EDGE,"E13.8.8"),sQuery(id+"F0.wireOp",EDGE,"E13.8.9"),sQuery(id+"F0.wireOp",EDGE,"E13.9.0"),sQuery(id+"F0.wireOp",EDGE,"E13.9.1"),sQuery(id+"F0.wireOp",EDGE,"E13.9.2"),sQuery(id+"F0.wireOp",EDGE,"E13.9.3"),sQuery(id+"F0.wireOp",EDGE,"E13.9.4"),sQuery(id+"F0.wireOp",EDGE,"E13.9.5"),sQuery(id+"F0.wireOp",EDGE,"E13.9.6"),sQuery(id+"F0.wireOp",EDGE,"E13.9.7"),sQuery(id+"F0.wireOp",EDGE,"E13.9.8"),sQuery(id+"F0.wireOp",EDGE,"E13.9.9"),sQuery(id+"F0.wireOp",EDGE,"E13.10.0"),sQuery(id+"F0.wireOp",EDGE,"E13.10.1"),sQuery(id+"F0.wireOp",EDGE,"E13.10.2"),sQuery(id+"F0.wireOp",EDGE,"E13.10.3"),sQuery(id+"F0.wireOp",EDGE,"E13.10.4"),sQuery(id+"F0.wireOp",EDGE,"E13.10.5"),sQuery(id+"F0.wireOp",EDGE,"E13.10.6"),sQuery(id+"F0.wireOp",EDGE,"E13.10.7"),sQuery(id+"F0.wireOp",EDGE,"E13.10.8"),sQuery(id+"F0.wireOp",EDGE,"E13.10.9"),sQuery(id+"F0.wireOp",EDGE,"E13.11.0"),sQuery(id+"F0.wireOp",EDGE,"E13.11.1"),sQuery(id+"F0.wireOp",EDGE,"E13.11.2"),sQuery(id+"F0.wireOp",EDGE,"E13.11.3"),sQuery(id+"F0.wireOp",EDGE,"E13.11.4"),sQuery(id+"F0.wireOp",EDGE,"E13.11.5"),sQuery(id+"F0.wireOp",EDGE,"E13.11.6"),sQuery(id+"F0.wireOp",EDGE,"E13.11.7"),sQuery(id+"F0.wireOp",EDGE,"E13.11.8"),sQuery(id+"F0.wireOp",EDGE,"E13.11.9"),sQuery(id+"F0.wireOp",EDGE,"E13.12.0"),sQuery(id+"F0.wireOp",EDGE,"E13.12.1"),sQuery(id+"F0.wireOp",EDGE,"E13.12.2"),sQuery(id+"F0.wireOp",EDGE,"E13.12.3"),sQuery(id+"F0.wireOp",EDGE,"E13.12.4"),sQuery(id+"F0.wireOp",EDGE,"E13.12.5"),sQuery(id+"F0.wireOp",EDGE,"E13.12.6"),sQuery(id+"F0.wireOp",EDGE,"E13.12.7"),sQuery(id+"F0.wireOp",EDGE,"E13.12.8"),sQuery(id+"F0.wireOp",EDGE,"E13.12.9"),sQuery(id+"F0.wireOp",EDGE,"E13.13.0"),sQuery(id+"F0.wireOp",EDGE,"E13.13.1"),sQuery(id+"F0.wireOp",EDGE,"E13.13.2"),sQuery(id+"F0.wireOp",EDGE,"E13.13.3"),sQuery(id+"F0.wireOp",EDGE,"E13.13.4"),sQuery(id+"F0.wireOp",EDGE,"E13.13.5"),sQuery(id+"F0.wireOp",EDGE,"E13.13.6"),sQuery(id+"F0.wireOp",EDGE,"E13.13.7"),sQuery(id+"F0.wireOp",EDGE,"E13.13.8"),sQuery(id+"F0.wireOp",EDGE,"E13.13.9"),sQuery(id+"F0.wireOp",EDGE,"E13.14.0"),sQuery(id+"F0.wireOp",EDGE,"E13.14.1"),sQuery(id+"F0.wireOp",EDGE,"E13.14.2"),sQuery(id+"F0.wireOp",EDGE,"E13.14.3"),sQuery(id+"F0.wireOp",EDGE,"E13.14.4"),sQuery(id+"F0.wireOp",EDGE,"E13.14.5"),sQuery(id+"F0.wireOp",EDGE,"E13.14.6"),sQuery(id+"F0.wireOp",EDGE,"E13.14.7"),sQuery(id+"F0.wireOp",EDGE,"E13.14.8"),sQuery(id+"F0.wireOp",EDGE,"E13.14.9"),sQuery(id+"F0.wireOp",EDGE,"E13.15.0"),sQuery(id+"F0.wireOp",EDGE,"E13.15.1"),sQuery(id+"F0.wireOp",EDGE,"E13.15.2"),sQuery(id+"F0.wireOp",EDGE,"E13.15.3"),sQuery(id+"F0.wireOp",EDGE,"E13.15.4"),sQuery(id+"F0.wireOp",EDGE,"E13.15.5"),sQuery(id+"F0.wireOp",EDGE,"E13.15.6"),sQuery(id+"F0.wireOp",EDGE,"E13.15.7"),sQuery(id+"F0.wireOp",EDGE,"E13.15.8"),sQuery(id+"F0.wireOp",EDGE,"E13.15.9"),sQuery(id+"F0.wireOp",EDGE,"E13.16.0"),sQuery(id+"F0.wireOp",EDGE,"E13.16.1"),sQuery(id+"F0.wireOp",EDGE,"E13.16.2"),sQuery(id+"F0.wireOp",EDGE,"E13.16.3"),sQuery(id+"F0.wireOp",EDGE,"E13.16.4"),sQuery(id+"F0.wireOp",EDGE,"E13.16.5"),sQuery(id+"F0.wireOp",EDGE,"E13.16.6"),sQuery(id+"F0.wireOp",EDGE,"E13.16.7"),sQuery(id+"F0.wireOp",EDGE,"E13.16.8"),sQuery(id+"F0.wireOp",EDGE,"E13.16.9"),sQuery(id+"F0.wireOp",EDGE,"E13.17.0"),sQuery(id+"F0.wireOp",EDGE,"E13.17.1"),sQuery(id+"F0.wireOp",EDGE,"E13.17.2"),sQuery(id+"F0.wireOp",EDGE,"E13.17.3"),sQuery(id+"F0.wireOp",EDGE,"E13.17.4"),sQuery(id+"F0.wireOp",EDGE,"E13.17.5"),sQuery(id+"F0.wireOp",EDGE,"E13.17.6"),sQuery(id+"F0.wireOp",EDGE,"E13.17.7"),sQuery(id+"F0.wireOp",EDGE,"E13.17.8"),sQuery(id+"F0.wireOp",EDGE,"E13.17.9"),sQuery(id+"F0.wireOp",EDGE,"E13.18.0"),sQuery(id+"F0.wireOp",EDGE,"E13.18.1"),sQuery(id+"F0.wireOp",EDGE,"E13.18.2"),sQuery(id+"F0.wireOp",EDGE,"E13.18.3"),sQuery(id+"F0.wireOp",EDGE,"E13.18.4"),sQuery(id+"F0.wireOp",EDGE,"E13.18.5"),sQuery(id+"F0.wireOp",EDGE,"E13.18.6"),sQuery(id+"F0.wireOp",EDGE,"E13.18.7"),sQuery(id+"F0.wireOp",EDGE,"E13.18.8"),sQuery(id+"F0.wireOp",EDGE,"E13.18.9"),sQuery(id+"F0.wireOp",EDGE,"E13.19.0"),sQuery(id+"F0.wireOp",EDGE,"E13.19.1"),sQuery(id+"F0.wireOp",EDGE,"E13.19.2"),sQuery(id+"F0.wireOp",EDGE,"E13.19.3"),sQuery(id+"F0.wireOp",EDGE,"E13.19.4"),sQuery(id+"F0.wireOp",EDGE,"E13.19.5"),sQuery(id+"F0.wireOp",EDGE,"E13.19.6"),sQuery(id+"F0.wireOp",EDGE,"E13.19.7"),sQuery(id+"F0.wireOp",EDGE,"E13.19.8"),sQuery(id+"F0.wireOp",EDGE,"E13.19.9"),sQuery(id+"F0.wireOp",EDGE,"E13.20.0"),sQuery(id+"F0.wireOp",EDGE,"E13.20.1"),sQuery(id+"F0.wireOp",EDGE,"E13.20.2"),sQuery(id+"F0.wireOp",EDGE,"E13.20.3"),sQuery(id+"F0.wireOp",EDGE,"E13.20.4"),sQuery(id+"F0.wireOp",EDGE,"E13.20.5"),sQuery(id+"F0.wireOp",EDGE,"E13.20.6"),sQuery(id+"F0.wireOp",EDGE,"E13.20.7"),sQuery(id+"F0.wireOp",EDGE,"E13.20.8"),sQuery(id+"F0.wireOp",EDGE,"E13.20.9"),sQuery(id+"F0.wireOp",EDGE,"E13.21.0"),sQuery(id+"F0.wireOp",EDGE,"E13.21.1"),sQuery(id+"F0.wireOp",EDGE,"E13.21.2"),sQuery(id+"F0.wireOp",EDGE,"E13.21.3"),sQuery(id+"F0.wireOp",EDGE,"E13.21.4"),sQuery(id+"F0.wireOp",EDGE,"E13.21.5"),sQuery(id+"F0.wireOp",EDGE,"E13.21.6"),sQuery(id+"F0.wireOp",EDGE,"E13.21.7"),sQuery(id+"F0.wireOp",EDGE,"E13.21.8"),sQuery(id+"F0.wireOp",EDGE,"E13.21.9"),sQuery(id+"F0.wireOp",EDGE,"E13.22.0"),sQuery(id+"F0.wireOp",EDGE,"E13.22.1"),sQuery(id+"F0.wireOp",EDGE,"E13.22.2"),sQuery(id+"F0.wireOp",EDGE,"E13.22.3"),sQuery(id+"F0.wireOp",EDGE,"E13.22.4"),sQuery(id+"F0.wireOp",EDGE,"E13.22.5"),sQuery(id+"F0.wireOp",EDGE,"E13.22.6"),sQuery(id+"F0.wireOp",EDGE,"E13.22.7"),sQuery(id+"F0.wireOp",EDGE,"E13.22.8"),sQuery(id+"F0.wireOp",EDGE,"E13.22.9"),sQuery(id+"F0.wireOp",EDGE,"E13.23.0"),sQuery(id+"F0.wireOp",EDGE,"E13.23.1"),sQuery(id+"F0.wireOp",EDGE,"E13.23.2"),sQuery(id+"F0.wireOp",EDGE,"E13.23.3"),sQuery(id+"F0.wireOp",EDGE,"E13.23.4"),sQuery(id+"F0.wireOp",EDGE,"E13.23.5"),sQuery(id+"F0.wireOp",EDGE,"E13.23.6"),sQuery(id+"F0.wireOp",EDGE,"E13.23.7"),sQuery(id+"F0.wireOp",EDGE,"E13.23.8"),sQuery(id+"F0.wireOp",EDGE,"E13.23.9"),sQuery(id+"F0.wireOp",EDGE,"E13.24.0"),sQuery(id+"F0.wireOp",EDGE,"E13.24.1"),sQuery(id+"F0.wireOp",EDGE,"E13.24.2"),sQuery(id+"F0.wireOp",EDGE,"E13.24.3"),sQuery(id+"F0.wireOp",EDGE,"E13.24.4"),sQuery(id+"F0.wireOp",EDGE,"E13.24.5"),sQuery(id+"F0.wireOp",EDGE,"E13.24.6"),sQuery(id+"F0.wireOp",EDGE,"E13.24.7"),sQuery(id+"F0.wireOp",EDGE,"E13.24.8"),sQuery(id+"F0.wireOp",EDGE,"E13.24.9"),sQuery(id+"F0.wireOp",EDGE,"E13.25.0"),sQuery(id+"F0.wireOp",EDGE,"E13.25.1"),sQuery(id+"F0.wireOp",EDGE,"E13.25.2"),sQuery(id+"F0.wireOp",EDGE,"E13.25.3"),sQuery(id+"F0.wireOp",EDGE,"E13.25.4"),sQuery(id+"F0.wireOp",EDGE,"E13.25.5"),sQuery(id+"F0.wireOp",EDGE,"E13.25.6"),sQuery(id+"F0.wireOp",EDGE,"E13.25.7"),sQuery(id+"F0.wireOp",EDGE,"E13.25.8"),sQuery(id+"F0.wireOp",EDGE,"E13.25.9"),sQuery(id+"F0.wireOp",EDGE,"E13.26.0"),sQuery(id+"F0.wireOp",EDGE,"E13.26.1"),sQuery(id+"F0.wireOp",EDGE,"E13.26.2"),sQuery(id+"F0.wireOp",EDGE,"E13.26.3"),sQuery(id+"F0.wireOp",EDGE,"E13.26.4"),sQuery(id+"F0.wireOp",EDGE,"E13.26.5"),sQuery(id+"F0.wireOp",EDGE,"E13.26.6"),sQuery(id+"F0.wireOp",EDGE,"E13.26.7"),sQuery(id+"F0.wireOp",EDGE,"E13.26.8"),sQuery(id+"F0.wireOp",EDGE,"E13.26.9"),sQuery(id+"F0.wireOp",EDGE,"E13.27.0"),sQuery(id+"F0.wireOp",EDGE,"E13.27.1"),sQuery(id+"F0.wireOp",EDGE,"E13.27.2"),sQuery(id+"F0.wireOp",EDGE,"E13.27.3"),sQuery(id+"F0.wireOp",EDGE,"E13.27.4"),sQuery(id+"F0.wireOp",EDGE,"E13.27.5"),sQuery(id+"F0.wireOp",EDGE,"E13.27.6"),sQuery(id+"F0.wireOp",EDGE,"E13.27.7"),sQuery(id+"F0.wireOp",EDGE,"E13.27.8"),sQuery(id+"F0.wireOp",EDGE,"E13.27.9"),sQuery(id+"F0.wireOp",EDGE,"E13.28.0"),sQuery(id+"F0.wireOp",EDGE,"E13.28.1"),sQuery(id+"F0.wireOp",EDGE,"E13.28.2"),sQuery(id+"F0.wireOp",EDGE,"E13.28.3"),sQuery(id+"F0.wireOp",EDGE,"E13.28.4"),sQuery(id+"F0.wireOp",EDGE,"E13.28.5"),sQuery(id+"F0.wireOp",EDGE,"E13.28.6"),sQuery(id+"F0.wireOp",EDGE,"E13.28.7"),sQuery(id+"F0.wireOp",EDGE,"E13.28.8"),sQuery(id+"F0.wireOp",EDGE,"E13.28.9"),sQuery(id+"F0.wireOp",EDGE,"E13.29.0"),sQuery(id+"F0.wireOp",EDGE,"E13.29.1"),sQuery(id+"F0.wireOp",EDGE,"E13.29.2"),sQuery(id+"F0.wireOp",EDGE,"E13.29.3"),sQuery(id+"F0.wireOp",EDGE,"E13.29.4"),sQuery(id+"F0.wireOp",EDGE,"E13.29.5"),sQuery(id+"F0.wireOp",EDGE,"E13.29.6"),sQuery(id+"F0.wireOp",EDGE,"E13.29.7"),sQuery(id+"F0.wireOp",EDGE,"E13.29.8"),sQuery(id+"F0.wireOp",EDGE,"E13.29.9"),sQuery(id+"F0.wireOp",EDGE,"E13.30.0"),sQuery(id+"F0.wireOp",EDGE,"E13.30.1"),sQuery(id+"F0.wireOp",EDGE,"E13.30.2"),sQuery(id+"F0.wireOp",EDGE,"E13.30.3"),sQuery(id+"F0.wireOp",EDGE,"E13.30.4"),sQuery(id+"F0.wireOp",EDGE,"E13.30.5"),sQuery(id+"F0.wireOp",EDGE,"E13.30.6"),sQuery(id+"F0.wireOp",EDGE,"E13.30.7"),sQuery(id+"F0.wireOp",EDGE,"E13.30.8"),sQuery(id+"F0.wireOp",EDGE,"E13.30.9"),sQuery(id+"F0.wireOp",EDGE,"E13.31.0"),sQuery(id+"F0.wireOp",EDGE,"E13.31.1"),sQuery(id+"F0.wireOp",EDGE,"E13.31.2"),sQuery(id+"F0.wireOp",EDGE,"E13.31.3"),sQuery(id+"F0.wireOp",EDGE,"E13.31.4"),sQuery(id+"F0.wireOp",EDGE,"E13.31.5"),sQuery(id+"F0.wireOp",EDGE,"E13.31.6"),sQuery(id+"F0.wireOp",EDGE,"E13.31.7"),sQuery(id+"F0.wireOp",EDGE,"E13.31.8"),sQuery(id+"F0.wireOp",EDGE,"E13.31.9"),sQuery(id+"F0.wireOp",EDGE,"E13.32.0"),sQuery(id+"F0.wireOp",EDGE,"E13.32.1"),sQuery(id+"F0.wireOp",EDGE,"E13.32.2"),sQuery(id+"F0.wireOp",EDGE,"E13.32.3"),sQuery(id+"F0.wireOp",EDGE,"E13.32.4"),sQuery(id+"F0.wireOp",EDGE,"E13.32.5"),sQuery(id+"F0.wireOp",EDGE,"E13.32.6"),sQuery(id+"F0.wireOp",EDGE,"E13.32.7"),sQuery(id+"F0.wireOp",EDGE,"E13.32.8"),sQuery(id+"F0.wireOp",EDGE,"E13.32.9"),sQuery(id+"F0.wireOp",EDGE,"E13.33.0"),sQuery(id+"F0.wireOp",EDGE,"E13.33.1"),sQuery(id+"F0.wireOp",EDGE,"E13.33.2"),sQuery(id+"F0.wireOp",EDGE,"E13.33.3"),sQuery(id+"F0.wireOp",EDGE,"E13.33.4"),sQuery(id+"F0.wireOp",EDGE,"E13.33.5"),sQuery(id+"F0.wireOp",EDGE,"E13.33.6"),sQuery(id+"F0.wireOp",EDGE,"E13.33.7"),sQuery(id+"F0.wireOp",EDGE,"E13.33.8"),sQuery(id+"F0.wireOp",EDGE,"E13.33.9"),sQuery(id+"F0.wireOp",EDGE,"E13.34.0"),sQuery(id+"F0.wireOp",EDGE,"E13.34.1"),sQuery(id+"F0.wireOp",EDGE,"E13.34.2"),sQuery(id+"F0.wireOp",EDGE,"E13.34.3"),sQuery(id+"F0.wireOp",EDGE,"E13.34.4"),sQuery(id+"F0.wireOp",EDGE,"E13.34.5"),sQuery(id+"F0.wireOp",EDGE,"E13.34.6"),sQuery(id+"F0.wireOp",EDGE,"E13.34.7"),sQuery(id+"F0.wireOp",EDGE,"E13.34.8"),sQuery(id+"F0.wireOp",EDGE,"E13.34.9"),sQuery(id+"F0.wireOp",EDGE,"E13.35.0"),sQuery(id+"F0.wireOp",EDGE,"E13.35.1"),sQuery(id+"F0.wireOp",EDGE,"E13.35.2"),sQuery(id+"F0.wireOp",EDGE,"E13.35.3"),sQuery(id+"F0.wireOp",EDGE,"E13.35.4"),sQuery(id+"F0.wireOp",EDGE,"E13.35.5"),sQuery(id+"F0.wireOp",EDGE,"E13.35.6"),sQuery(id+"F0.wireOp",EDGE,"E13.35.7"),sQuery(id+"F0.wireOp",EDGE,"E13.35.8"),sQuery(id+"F0.wireOp",EDGE,"E13.35.9"),sQuery(id+"F0.wireOp",EDGE,"E14.trimOffspring"),sQuery(id+"F0.wireOp",EDGE,"E15.trimOffspring"),sQuery(id+"F0.wireOp",EDGE,"E16.trimOffspring"),sQuery(id+"F0.wireOp",EDGE,"E17.trimOffspring"),sQuery(id+"F0.wireOp",EDGE,"E18.trimOffspring"),sQuery(id+"F0.wireOp",EDGE,"E19.trimOffspring"),sQuery(id+"F0.wireOp",EDGE,"E20.trimOffspring"),sQuery(id+"F0.wireOp",EDGE,"E21.trimOffspring"),sQuery(id+"F0.wireOp",EDGE,"E22.trimOffspring"),sQuery(id+"F0.wireOp",EDGE,"E23.trimOffspring"),sQuery(id+"F0.wireOp",EDGE,"E24.trimOffspring"),sQuery(id+"F0.wireOp",EDGE,"E25.trimOffspring"),sQuery(id+"F0.wireOp",EDGE,"E26.trimOffspring"),sQuery(id+"F0.wireOp",EDGE,"E27.trimOffspring"),sQuery(id+"F0.wireOp",EDGE,"E28.trimOffspring"),sQuery(id+"F0.wireOp",EDGE,"E29.trimOffspring"),sQuery(id+"F0.wireOp",EDGE,"E30.trimOffspring"),sQuery(id+"F0.wireOp",EDGE,"E31.trimOffspring"),sQuery(id+"F0.wireOp",EDGE,"E32.trimOffspring"),sQuery(id+"F0.wireOp",EDGE,"E33.trimOffspring"),sQuery(id+"F0.wireOp",EDGE,"E34.trimOffspring"),sQuery(id+"F0.wireOp",EDGE,"E35.trimOffspring"),sQuery(id+"F0.wireOp",EDGE,"E36.trimOffspring"),sQuery(id+"F0.wireOp",EDGE,"E37.trimOffspring"),sQuery(id+"F0.wireOp",EDGE,"E38.trimOffspring"),sQuery(id+"F0.wireOp",EDGE,"E39.trimOffspring"),sQuery(id+"F0.wireOp",EDGE,"E40.trimOffspring"),sQuery(id+"F0.wireOp",EDGE,"E41.trimOffspring"),sQuery(id+"F0.wireOp",EDGE,"E42.trimOffspring"),sQuery(id+"F0.wireOp",EDGE,"E43.trimOffspring"),sQuery(id+"F0.wireOp",EDGE,"E44.trimOffspring"),sQuery(id+"F0.wireOp",EDGE,"E45.trimOffspring"),sQuery(id+"F0.wireOp",EDGE,"E46.trimOffspring"),sQuery(id+"F0.wireOp",EDGE,"E47.trimOffspring"),sQuery(id+"F0.wireOp",EDGE,"E48.trimOffspring"),sQuery(id+"F0.wireOp",EDGE,"E49"),sQuery(id+"F0.wireOp",EDGE,"E50"),sQuery(id+"F0.wireOp",EDGE,"E51"),sQuery(id+"F0.wireOp",EDGE,"E52"),sQuery(id+"F0.wireOp",EDGE,"E53"),sQuery(id+"F0.wireOp",EDGE,"E54"),sQuery(id+"F0.wireOp",EDGE,"E55"),sQuery(id+"F0.wireOp",EDGE,"E56"),sQuery(id+"F0.wireOp",EDGE,"E57"),sQuery(id+"F0.wireOp",EDGE,"E58"),sQuery(id+"F0.wireOp",EDGE,"E59"),sQuery(id+"F0.wireOp",EDGE,"E60"),sQuery(id+"F0.wireOp",EDGE,"E61"),sQuery(id+"F0.wireOp",EDGE,"E62"),sQuery(id+"F0.wireOp",EDGE,"E63"),sQuery(id+"F0.wireOp",EDGE,"E64"),sQuery(id+"F0.wireOp",EDGE,"E65"),sQuery(id+"F0.wireOp",EDGE,"E66"),sQuery(id+"F0.wireOp",EDGE,"E67"),sQuery(id+"F0.wireOp",EDGE,"E68"),sQuery(id+"F0.wireOp",EDGE,"E69"),sQuery(id+"F0.wireOp",EDGE,"E70"),sQuery(id+"F0.wireOp",EDGE,"E71"),sQuery(id+"F0.wireOp",EDGE,"E72"),sQuery(id+"F0.wireOp",EDGE,"E73"),sQuery(id+"F0.wireOp",EDGE,"E74"),sQuery(id+"F0.wireOp",EDGE,"E75"),sQuery(id+"F0.wireOp",EDGE,"E76"),sQuery(id+"F0.wireOp",EDGE,"E77"),sQuery(id+"F0.wireOp",EDGE,"E78"),sQuery(id+"F0.wireOp",EDGE,"E79"),sQuery(id+"F0.wireOp",EDGE,"E80"),sQuery(id+"F0.wireOp",EDGE,"E81"),sQuery(id+"F0.wireOp",EDGE,"E82"),sQuery(id+"F0.wireOp",EDGE,"E83")])]});
            hole(context, id + "F3", {"style" : HoleStyle.SIMPLE, "endStyle" : HoleEndStyle.THROUGH, "holeDiameter" : 12.7 * mm, "tappedDepth" : 12.7 * mm, "tapClearance" : 3, "locations" : qUnion([Q0]), "scope" : qUnion([Q1])});
        }
    });
